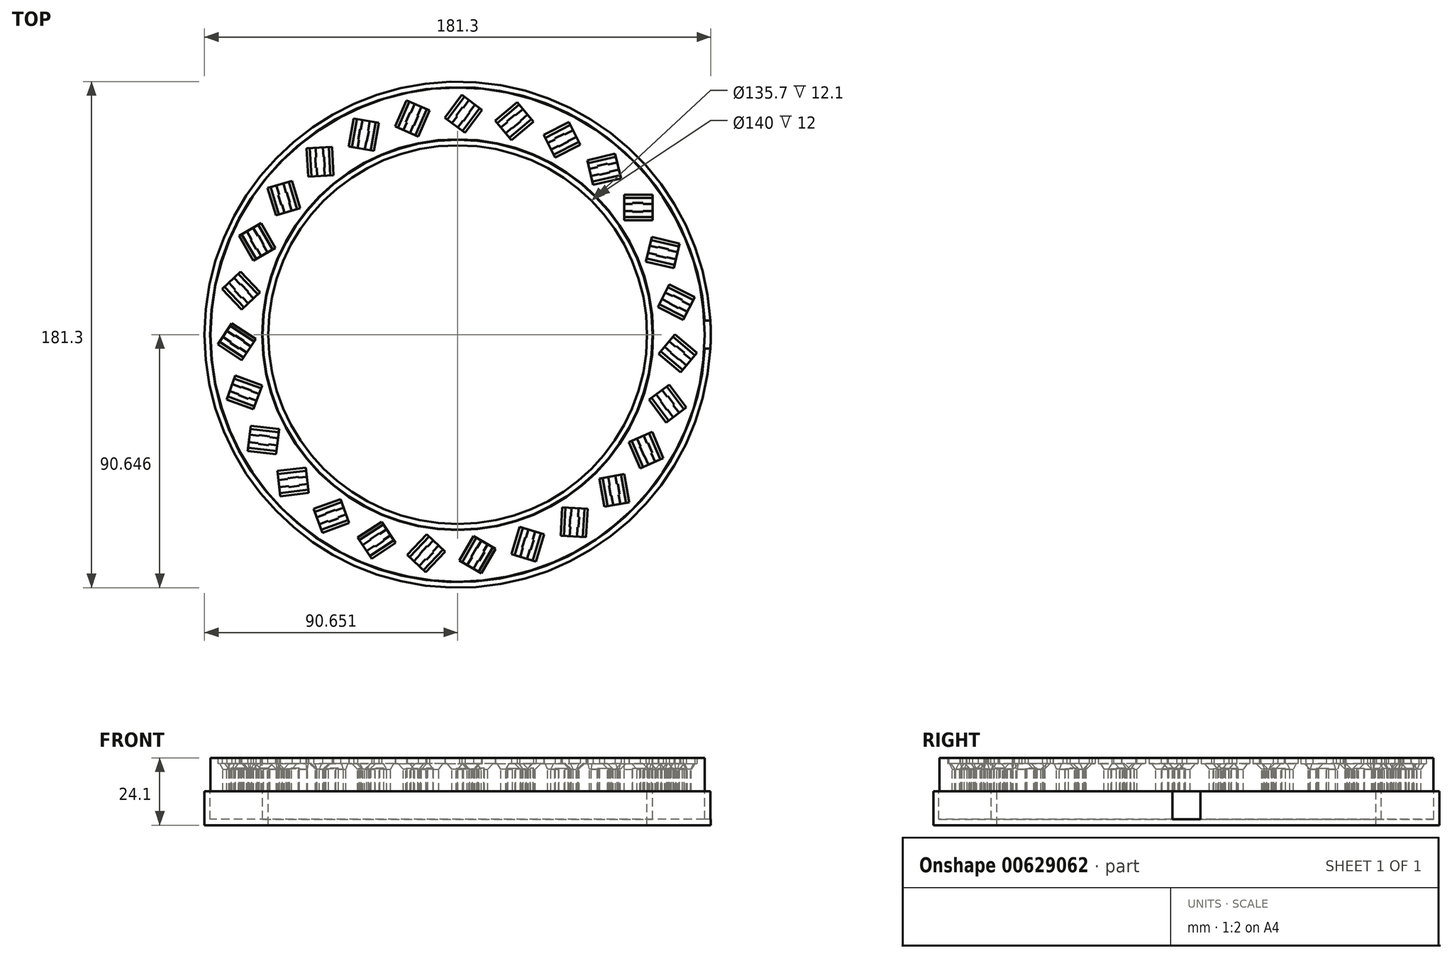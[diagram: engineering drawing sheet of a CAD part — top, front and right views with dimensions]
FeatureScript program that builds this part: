
annotation { "Feature Type Name" : "Feature", "Feature Type Description" : "" }
export const myFeature = defineFeature(function(context is Context, id is Id, definition is map)
    precondition{}
    {
        {
            var Q0;
            Q0=qCreatedBy(makeId("Top.planeOp"),FACE);
            var sketch = newSketch(context, id + "F0", { "sketchPlane" : qUnion([Q0])});
            skLineSegment(sketch, "E0.bottom", {"start": v(0, 0) * mm, "end": v(10.2, 0) * mm});
            skLineSegment(sketch, "E0.top", {"start": v(0, 9.1) * mm, "end": v(10.2, 9.1) * mm});
            skLineSegment(sketch, "E0.left", {"start": v(0, 0) * mm, "end": v(0, 9.1) * mm});
            skLineSegment(sketch, "E0.right", {"start": v(10.2, 0) * mm, "end": v(10.2, 9.1) * mm});
            skLineSegment(sketch, "E1.0", {"start": v(-3.5, 12.6) * mm, "end": v(13.7, 12.6) * mm});
            skLineSegment(sketch, "E1.1", {"start": v(-3.5, -3.5) * mm, "end": v(-3.5, 12.6) * mm});
            skLineSegment(sketch, "E1.2", {"start": v(-3.5, -3.5) * mm, "end": v(13.7, -3.5) * mm});
            skLineSegment(sketch, "E1.3", {"start": v(13.7, -3.5) * mm, "end": v(13.7, 12.6) * mm});
            skSolve(sketch);
        }
        {
            var Q0;
            Q0=makeQuery(id+"F0.imprint","IMPRINT",FACE,{"disambiguationData":[TD([[makeQuery(id+"F0.imprint","IMPRINT",EDGE,{"derivedFrom":sQuery(id+"F0.wireOp",EDGE,"E0.bottom")}),-1.0]])]});
            extrude(context, id + "F1", {"entities" : qUnion([Q0]), "depth" : 2 * mm, "offsetDistance" : 25 * mm});
        }
        {
            var Q0;
            Q0=makeQuery(id+"F1.opExtrude","CAP_FACE",FACE,{"disambiguationData":[OSD([sQuery(id+"F0.wireOp",EDGE,"E0.bottom"),sQuery(id+"F0.wireOp",EDGE,"E0.top"),sQuery(id+"F0.wireOp",EDGE,"E0.left"),sQuery(id+"F0.wireOp",EDGE,"E0.right"),sQuery(id+"F0.wireOp",EDGE,"E1.0"),sQuery(id+"F0.wireOp",EDGE,"E1.1"),sQuery(id+"F0.wireOp",EDGE,"E1.2"),sQuery(id+"F0.wireOp",EDGE,"E1.3")])],"isStart":true});
            var sketch = newSketch(context, id + "F2", { "sketchPlane" : qUnion([Q0])});
            skLineSegment(sketch, "E2.0", {"start": v(0, -5.85) * mm, "end": v(10.2, -5.85) * mm});
            skLineSegment(sketch, "E3.0", {"start": v(0, -3.25) * mm, "end": v(10.2, -3.25) * mm});
            skPoint(sketch, "E4.end.orphan", {"position": v(10.2, -4.55) * mm});
            skPoint(sketch, "E4.start.orphan", {"position": v(0, -4.55) * mm});
            skLineSegment(sketch, "E5.0", {"start": v(10.2, 0) * mm, "end": v(10.2, -9.1) * mm});
            skSolve(sketch);
        }
        {
            var Q0;
            {var subQ0=sQuery(id+"F2.wireOp",EDGE,"E3.0");Q0=makeQuery(id+"F2.imprint","IMPRINT",FACE,{"disambiguationData":[TD([[makeQuery(id+"F2.imprint","IMPRINT",EDGE,{"derivedFrom":subQ0}),1.0]])]});}
            var Q1;
            {var subQ0=sQuery(id+"F2.wireOp",EDGE,"E2.0");Q1=makeQuery(id+"F2.imprint","IMPRINT",FACE,{"disambiguationData":[TD([[makeQuery(id+"F2.imprint","IMPRINT",EDGE,{"derivedFrom":subQ0}),-1.0]])]});}
            var Q2;
            {var subQ1=makeQuery(id+"F1.opExtrude","CAP_EDGE",EDGE,{"disambiguationData":[OSD([sQuery(id+"F0.wireOp",EDGE,"E0.bottom")])],"isStart":true});Q2=makeQuery(id+"F2.imprint","IMPRINT",FACE,{"disambiguationData":[TD([[makeQuery(id+"F2.imprint","IMPRINT",EDGE,{"derivedFrom":subQ1}),1.0]])]});}
            extrude(context, id + "F3", {"entities" : qUnion([Q0, Q1, Q2]), "operationType" : NewBodyOperationType.ADD, "depth" : 10 * mm, "offsetDistance" : 25 * mm});
        }
        {
            var Q0;
            Q0=makeQuery(id+"F3.opExtrude","CAP_EDGE",EDGE,{"disambiguationData":[OSD([sQuery(id+"F2.wireOp",EDGE,"E3.0")])],"isStart":true});
            var Q1;
            Q1=makeQuery(id+"F3.opExtrude","CAP_EDGE",EDGE,{"disambiguationData":[OSD([sQuery(id+"F2.wireOp",EDGE,"E2.0")])],"isStart":true});
            chamfer(context, id + "F4", {"entities" : qUnion([Q0, Q1]), "width" : 2.1 * mm, "tangentPropagation" : true});
        }
        {
            var Q0;
            Q0=makeQuery(id+"F1.opExtrude","CAP_FACE",FACE,{"disambiguationData":[OSD([sQuery(id+"F0.wireOp",EDGE,"E0.bottom"),sQuery(id+"F0.wireOp",EDGE,"E0.top"),sQuery(id+"F0.wireOp",EDGE,"E0.left"),sQuery(id+"F0.wireOp",EDGE,"E0.right"),sQuery(id+"F0.wireOp",EDGE,"E1.0"),sQuery(id+"F0.wireOp",EDGE,"E1.1"),sQuery(id+"F0.wireOp",EDGE,"E1.2"),sQuery(id+"F0.wireOp",EDGE,"E1.3")])],"isStart":false});
            var sketch = newSketch(context, id + "F5", { "sketchPlane" : qUnion([Q0])});
            skLineSegment(sketch, "E6.bottom", {"start": v(3.03, 6.2) * mm, "end": v(6.78, 6.2) * mm});
            skLineSegment(sketch, "E6.top", {"start": v(3.03, 3) * mm, "end": v(6.78, 3) * mm});
            skLineSegment(sketch, "E6.left", {"start": v(3.03, 6.2) * mm, "end": v(3.03, 3) * mm});
            skLineSegment(sketch, "E6.right", {"start": v(6.78, 6.2) * mm, "end": v(6.78, 3) * mm});
            skLineSegment(sketch, "E7.0", {"start": v(10.2, 5.85) * mm, "end": v(0, 5.85) * mm});
            skSolve(sketch);
        }
        {
            var Q0;
            {var subQ0=sQuery(id+"F5.wireOp",EDGE,"E6.bottom");Q0=makeQuery(id+"F5.imprint","IMPRINT",FACE,{"disambiguationData":[TD([[makeQuery(id+"F5.imprint","IMPRINT",EDGE,{"derivedFrom":subQ0}),-1.0]])]});}
            var Q1;
            {var subQ0=sQuery(id+"F5.wireOp",EDGE,"E6.top");Q1=makeQuery(id+"F5.imprint","IMPRINT",FACE,{"disambiguationData":[TD([[makeQuery(id+"F5.imprint","IMPRINT",EDGE,{"derivedFrom":subQ0}),1.0]])]});}
            extrude(context, id + "F6", {"entities" : qUnion([Q0, Q1]), "operationType" : NewBodyOperationType.REMOVE, "oppositeDirection" : true, "depth" : 25 * mm, "offsetDistance" : 25 * mm});
        }
        {
            var Q0;
            Q0=makeQuery(id+"F1.opExtrude","CAP_FACE",FACE,{"disambiguationData":[OSD([sQuery(id+"F0.wireOp",EDGE,"E0.bottom"),sQuery(id+"F0.wireOp",EDGE,"E0.top"),sQuery(id+"F0.wireOp",EDGE,"E0.left"),sQuery(id+"F0.wireOp",EDGE,"E0.right"),sQuery(id+"F0.wireOp",EDGE,"E1.0"),sQuery(id+"F0.wireOp",EDGE,"E1.1"),sQuery(id+"F0.wireOp",EDGE,"E1.2"),sQuery(id+"F0.wireOp",EDGE,"E1.3")])],"isStart":false});
            var sketch = newSketch(context, id + "F7", { "sketchPlane" : qUnion([Q0])});
            skCircle(sketch, "E8", {"center": v(-59.6, -41.02) * mm, "radius": 67.5 * mm});
            skSolve(sketch);
        }
        {
            var Q0;
            Q0=makeQuery(id+"F1.opExtrude","SWEPT_BODY",BODY,{"disambiguationData":[OSD([sQuery(id+"F0.wireOp",EDGE,"E0.bottom"),sQuery(id+"F0.wireOp",EDGE,"E0.top"),sQuery(id+"F0.wireOp",EDGE,"E0.left"),sQuery(id+"F0.wireOp",EDGE,"E0.right"),sQuery(id+"F0.wireOp",EDGE,"E1.0"),sQuery(id+"F0.wireOp",EDGE,"E1.1"),sQuery(id+"F0.wireOp",EDGE,"E1.2"),sQuery(id+"F0.wireOp",EDGE,"E1.3")])]});
            var Q1;
            Q1=sQuery(id+"F7.wireOp",EDGE,"E8");
            circularPattern(context, id + "F8", {"entities" : qUnion([Q0]), "axis" : qUnion([Q1]), "angle" : 360 * degree, "instanceCount" : 27, "equalSpace" : true});
        }
        {
            var Q0;
            Q0=makeQuery(id+"F8.opPattern","COPY",FACE,{"derivedFrom":makeQuery(id+"F1.opExtrude","CAP_FACE",FACE,{"disambiguationData":[OSD([sQuery(id+"F0.wireOp",EDGE,"E0.bottom"),sQuery(id+"F0.wireOp",EDGE,"E0.top"),sQuery(id+"F0.wireOp",EDGE,"E0.left"),sQuery(id+"F0.wireOp",EDGE,"E0.right"),sQuery(id+"F0.wireOp",EDGE,"E1.0"),sQuery(id+"F0.wireOp",EDGE,"E1.1"),sQuery(id+"F0.wireOp",EDGE,"E1.2"),sQuery(id+"F0.wireOp",EDGE,"E1.3")])],"isStart":false}),"instanceName":"8"});
            var sketch = newSketch(context, id + "F9", { "sketchPlane" : qUnion([Q0])});
            skPoint(sketch, "E9.0", {"position": v(-59.6, -41.02) * mm});
            skPoint(sketch, "E10.0", {"position": v(-148.92, -24.5) * mm});
            skCircle(sketch, "E11", {"center": v(-59.6, -41.02) * mm, "radius": 90.83 * mm});
            skCircle(sketch, "E12.0", {"center": v(-59.6, -41.02) * mm, "radius": 67.5 * mm});
            skLineSegment(sketch, "E13.0.0", {"start": v(-111.65, 1.97) * mm, "end": v(-116.58, 18.44) * mm});
            skLineSegment(sketch, "E13.0.1", {"start": v(-116.58, 18.44) * mm, "end": v(-132, 13.83) * mm});
            skLineSegment(sketch, "E13.0.2", {"start": v(-132, 13.83) * mm, "end": v(-127.07, -2.65) * mm});
            skLineSegment(sketch, "E13.0.3", {"start": v(-127.07, -2.65) * mm, "end": v(-111.65, 1.97) * mm});
            skLineSegment(sketch, "E14.0.0", {"start": v(-120.16, -11.2) * mm, "end": v(-128.76, 3.7) * mm});
            skLineSegment(sketch, "E14.0.1", {"start": v(-128.76, 3.7) * mm, "end": v(-142.7, -4.35) * mm});
            skLineSegment(sketch, "E14.0.2", {"start": v(-142.7, -4.35) * mm, "end": v(-134.1, -19.24) * mm});
            skLineSegment(sketch, "E14.0.3", {"start": v(-134.1, -19.24) * mm, "end": v(-120.16, -11.2) * mm});
            skLineSegment(sketch, "E15.0.0", {"start": v(-125.4, -25.96) * mm, "end": v(-137.21, -13.45) * mm});
            skLineSegment(sketch, "E15.0.1", {"start": v(-137.21, -13.45) * mm, "end": v(-148.92, -24.5) * mm});
            skLineSegment(sketch, "E15.0.2", {"start": v(-148.92, -24.5) * mm, "end": v(-137.12, -37.01) * mm});
            skLineSegment(sketch, "E15.0.3", {"start": v(-137.12, -37.01) * mm, "end": v(-125.4, -25.96) * mm});
            skLineSegment(sketch, "E16.0.0", {"start": v(-127.1, -41.54) * mm, "end": v(-141.48, -32.1) * mm});
            skLineSegment(sketch, "E16.0.1", {"start": v(-141.48, -32.1) * mm, "end": v(-150.32, -45.54) * mm});
            skLineSegment(sketch, "E16.0.2", {"start": v(-150.32, -45.54) * mm, "end": v(-135.95, -55) * mm});
            skLineSegment(sketch, "E16.0.3", {"start": v(-135.95, -55) * mm, "end": v(-127.1, -41.54) * mm});
            skLineSegment(sketch, "E17.0.0", {"start": v(-125.17, -57.1) * mm, "end": v(-141.33, -51.21) * mm});
            skLineSegment(sketch, "E17.0.1", {"start": v(-141.33, -51.21) * mm, "end": v(-146.84, -66.34) * mm});
            skLineSegment(sketch, "E17.0.2", {"start": v(-146.84, -66.34) * mm, "end": v(-130.67, -72.22) * mm});
            skLineSegment(sketch, "E17.0.3", {"start": v(-130.67, -72.22) * mm, "end": v(-125.17, -57.1) * mm});
            skLineSegment(sketch, "E18.0.0", {"start": v(-119.7, -71.78) * mm, "end": v(-136.78, -69.78) * mm});
            skLineSegment(sketch, "E18.0.1", {"start": v(-136.78, -69.78) * mm, "end": v(-138.65, -85.78) * mm});
            skLineSegment(sketch, "E18.0.2", {"start": v(-138.65, -85.78) * mm, "end": v(-121.56, -87.77) * mm});
            skLineSegment(sketch, "E18.0.3", {"start": v(-121.56, -87.77) * mm, "end": v(-119.7, -71.78) * mm});
            skLineSegment(sketch, "E19.0.0", {"start": v(-110.98, -84.8) * mm, "end": v(-128.07, -86.8) * mm});
            skLineSegment(sketch, "E19.0.1", {"start": v(-128.07, -86.8) * mm, "end": v(-126.2, -102.8) * mm});
            skLineSegment(sketch, "E19.0.2", {"start": v(-126.2, -102.8) * mm, "end": v(-109.11, -100.8) * mm});
            skLineSegment(sketch, "E19.0.3", {"start": v(-109.11, -100.8) * mm, "end": v(-110.98, -84.8) * mm});
            skLineSegment(sketch, "E20.0.0", {"start": v(-99.5, -95.48) * mm, "end": v(-115.66, -101.36) * mm});
            skLineSegment(sketch, "E20.0.1", {"start": v(-115.66, -101.36) * mm, "end": v(-110.16, -116.49) * mm});
            skLineSegment(sketch, "E20.0.2", {"start": v(-110.16, -116.49) * mm, "end": v(-94, -110.6) * mm});
            skLineSegment(sketch, "E20.0.3", {"start": v(-94, -110.6) * mm, "end": v(-99.5, -95.48) * mm});
            skLineSegment(sketch, "E21.0.0", {"start": v(-85.87, -103.2) * mm, "end": v(-100.24, -112.66) * mm});
            skLineSegment(sketch, "E21.0.1", {"start": v(-100.24, -112.66) * mm, "end": v(-91.4, -126.11) * mm});
            skLineSegment(sketch, "E21.0.2", {"start": v(-91.4, -126.11) * mm, "end": v(-77.02, -116.66) * mm});
            skLineSegment(sketch, "E21.0.3", {"start": v(-77.02, -116.66) * mm, "end": v(-85.87, -103.2) * mm});
            skLineSegment(sketch, "E22.0.0", {"start": v(-70.82, -107.59) * mm, "end": v(-82.62, -120.1) * mm});
            skLineSegment(sketch, "E22.0.1", {"start": v(-82.62, -120.1) * mm, "end": v(-70.91, -131.15) * mm});
            skLineSegment(sketch, "E22.0.2", {"start": v(-70.91, -131.15) * mm, "end": v(-59.1, -118.64) * mm});
            skLineSegment(sketch, "E22.0.3", {"start": v(-59.1, -118.64) * mm, "end": v(-70.82, -107.59) * mm});
            skLineSegment(sketch, "E23.0.0", {"start": v(-55.17, -108.38) * mm, "end": v(-63.77, -123.27) * mm});
            skLineSegment(sketch, "E23.0.1", {"start": v(-63.77, -123.27) * mm, "end": v(-49.82, -131.32) * mm});
            skLineSegment(sketch, "E23.0.2", {"start": v(-49.82, -131.32) * mm, "end": v(-41.22, -116.43) * mm});
            skLineSegment(sketch, "E23.0.3", {"start": v(-41.22, -116.43) * mm, "end": v(-55.17, -108.38) * mm});
            skLineSegment(sketch, "E24.0.0", {"start": v(-39.75, -105.54) * mm, "end": v(-44.69, -122.02) * mm});
            skLineSegment(sketch, "E24.0.1", {"start": v(-44.69, -122.02) * mm, "end": v(-29.26, -126.63) * mm});
            skLineSegment(sketch, "E24.0.2", {"start": v(-29.26, -126.63) * mm, "end": v(-24.33, -110.16) * mm});
            skLineSegment(sketch, "E24.0.3", {"start": v(-24.33, -110.16) * mm, "end": v(-39.75, -105.54) * mm});
            skLineSegment(sketch, "E25.0.0", {"start": v(-25.41, -99.22) * mm, "end": v(-26.41, -116.4) * mm});
            skLineSegment(sketch, "E25.0.1", {"start": v(-26.41, -116.4) * mm, "end": v(-10.34, -117.33) * mm});
            skLineSegment(sketch, "E25.0.2", {"start": v(-10.34, -117.33) * mm, "end": v(-9.34, -100.16) * mm});
            skLineSegment(sketch, "E25.0.3", {"start": v(-9.34, -100.16) * mm, "end": v(-25.41, -99.22) * mm});
            skLineSegment(sketch, "E26.0.0", {"start": v(-12.91, -89.76) * mm, "end": v(-9.92, -106.7) * mm});
            skLineSegment(sketch, "E26.0.1", {"start": v(-9.92, -106.7) * mm, "end": v(5.93, -103.9) * mm});
            skLineSegment(sketch, "E26.0.2", {"start": v(5.93, -103.9) * mm, "end": v(2.94, -86.97) * mm});
            skLineSegment(sketch, "E26.0.3", {"start": v(2.94, -86.97) * mm, "end": v(-12.91, -89.76) * mm});
            skLineSegment(sketch, "E27.0.0", {"start": v(-2.93, -77.68) * mm, "end": v(3.88, -93.47) * mm});
            skLineSegment(sketch, "E27.0.1", {"start": v(3.88, -93.47) * mm, "end": v(18.67, -87.1) * mm});
            skLineSegment(sketch, "E27.0.2", {"start": v(18.67, -87.1) * mm, "end": v(11.85, -71.3) * mm});
            skLineSegment(sketch, "E27.0.3", {"start": v(11.85, -71.3) * mm, "end": v(-2.93, -77.68) * mm});
            skLineSegment(sketch, "E28.0.0", {"start": v(4, -63.62) * mm, "end": v(14.27, -77.42) * mm});
            skLineSegment(sketch, "E28.0.1", {"start": v(14.27, -77.42) * mm, "end": v(27.18, -67.8) * mm});
            skLineSegment(sketch, "E28.0.2", {"start": v(27.18, -67.8) * mm, "end": v(16.91, -54) * mm});
            skLineSegment(sketch, "E28.0.3", {"start": v(16.91, -54) * mm, "end": v(4, -63.62) * mm});
            skLineSegment(sketch, "E29.0.0", {"start": v(7.5, -48.34) * mm, "end": v(20.67, -59.4) * mm});
            skLineSegment(sketch, "E29.0.1", {"start": v(20.67, -59.4) * mm, "end": v(31.02, -47.07) * mm});
            skLineSegment(sketch, "E29.0.2", {"start": v(31.02, -47.07) * mm, "end": v(17.84, -36.01) * mm});
            skLineSegment(sketch, "E29.0.3", {"start": v(17.84, -36.01) * mm, "end": v(7.5, -48.34) * mm});
            skLineSegment(sketch, "E30.0.0", {"start": v(-3.5, 12.6) * mm, "end": v(-3.5, -3.5) * mm});
            skLineSegment(sketch, "E30.0.1", {"start": v(-3.5, -3.5) * mm, "end": v(13.7, -3.5) * mm});
            skLineSegment(sketch, "E30.0.2", {"start": v(13.7, -3.5) * mm, "end": v(13.7, 12.6) * mm});
            skLineSegment(sketch, "E30.0.3", {"start": v(13.7, 12.6) * mm, "end": v(-3.5, 12.6) * mm});
            skLineSegment(sketch, "E31.0.0", {"start": v(-13.67, 8.43) * mm, "end": v(3.07, 12.4) * mm});
            skLineSegment(sketch, "E31.0.1", {"start": v(3.07, 12.4) * mm, "end": v(-0.64, 28.06) * mm});
            skLineSegment(sketch, "E31.0.2", {"start": v(-0.64, 28.06) * mm, "end": v(-17.38, 24.1) * mm});
            skLineSegment(sketch, "E31.0.3", {"start": v(-17.38, 24.1) * mm, "end": v(-13.67, 8.43) * mm});
            skLineSegment(sketch, "E32.0.0", {"start": v(-26.3, 17.7) * mm, "end": v(-10.94, 25.4) * mm});
            skLineSegment(sketch, "E32.0.1", {"start": v(-10.94, 25.4) * mm, "end": v(-18.16, 39.8) * mm});
            skLineSegment(sketch, "E32.0.2", {"start": v(-18.16, 39.8) * mm, "end": v(-33.53, 32.08) * mm});
            skLineSegment(sketch, "E32.0.3", {"start": v(-33.53, 32.08) * mm, "end": v(-26.3, 17.7) * mm});
            skLineSegment(sketch, "E33.0.0", {"start": v(-40.75, 23.79) * mm, "end": v(-27.57, 34.84) * mm});
            skLineSegment(sketch, "E33.0.1", {"start": v(-27.57, 34.84) * mm, "end": v(-37.92, 47.18) * mm});
            skLineSegment(sketch, "E33.0.2", {"start": v(-37.92, 47.18) * mm, "end": v(-51.1, 36.12) * mm});
            skLineSegment(sketch, "E33.0.3", {"start": v(-51.1, 36.12) * mm, "end": v(-40.75, 23.79) * mm});
            skLineSegment(sketch, "E34.0.0", {"start": v(-56.2, 26.39) * mm, "end": v(-45.93, 40.19) * mm});
            skLineSegment(sketch, "E34.0.1", {"start": v(-45.93, 40.19) * mm, "end": v(-58.84, 49.8) * mm});
            skLineSegment(sketch, "E34.0.2", {"start": v(-58.84, 49.8) * mm, "end": v(-69.12, 36) * mm});
            skLineSegment(sketch, "E34.0.3", {"start": v(-69.12, 36) * mm, "end": v(-56.2, 26.39) * mm});
            skLineSegment(sketch, "E35.0.0", {"start": v(-71.84, 25.36) * mm, "end": v(-65.03, 41.15) * mm});
            skLineSegment(sketch, "E35.0.1", {"start": v(-65.03, 41.15) * mm, "end": v(-79.81, 47.53) * mm});
            skLineSegment(sketch, "E35.0.2", {"start": v(-79.81, 47.53) * mm, "end": v(-86.62, 31.74) * mm});
            skLineSegment(sketch, "E35.0.3", {"start": v(-86.62, 31.74) * mm, "end": v(-71.84, 25.36) * mm});
            skLineSegment(sketch, "E36.0.0", {"start": v(-86.82, 20.75) * mm, "end": v(-83.83, 37.69) * mm});
            skLineSegment(sketch, "E36.0.1", {"start": v(-83.83, 37.69) * mm, "end": v(-99.69, 40.48) * mm});
            skLineSegment(sketch, "E36.0.2", {"start": v(-99.69, 40.48) * mm, "end": v(-102.68, 23.54) * mm});
            skLineSegment(sketch, "E36.0.3", {"start": v(-102.68, 23.54) * mm, "end": v(-86.82, 20.75) * mm});
            skLineSegment(sketch, "E37.0.0", {"start": v(-100.33, 12.8) * mm, "end": v(-101.33, 29.98) * mm});
            skLineSegment(sketch, "E37.0.1", {"start": v(-101.33, 29.98) * mm, "end": v(-117.4, 29.04) * mm});
            skLineSegment(sketch, "E37.0.2", {"start": v(-117.4, 29.04) * mm, "end": v(-116.4, 11.87) * mm});
            skLineSegment(sketch, "E37.0.3", {"start": v(-116.4, 11.87) * mm, "end": v(-100.33, 12.8) * mm});
            skLineSegment(sketch, "E38.0.0", {"start": v(7.37, -32.67) * mm, "end": v(22.74, -40.4) * mm});
            skLineSegment(sketch, "E38.0.1", {"start": v(22.74, -40.4) * mm, "end": v(29.97, -26) * mm});
            skLineSegment(sketch, "E38.0.2", {"start": v(29.97, -26) * mm, "end": v(14.6, -18.29) * mm});
            skLineSegment(sketch, "E38.0.3", {"start": v(14.6, -18.29) * mm, "end": v(7.37, -32.67) * mm});
            skLineSegment(sketch, "E39.0.0", {"start": v(3.64, -17.45) * mm, "end": v(20.38, -21.42) * mm});
            skLineSegment(sketch, "E39.0.1", {"start": v(20.38, -21.42) * mm, "end": v(24.1, -5.75) * mm});
            skLineSegment(sketch, "E39.0.2", {"start": v(24.1, -5.75) * mm, "end": v(7.35, -1.79) * mm});
            skLineSegment(sketch, "E39.0.3", {"start": v(7.35, -1.79) * mm, "end": v(3.64, -17.45) * mm});
            skSolve(sketch);
        }
        {
            var Q0;
            {var subQ1=sQuery(id+"F9.wireOp",EDGE,"E19.0.2");Q0=makeQuery(id+"F9.imprint","IMPRINT",FACE,{"disambiguationData":[TD([[makeQuery(id+"F9.imprint","IMPRINT",EDGE,{"derivedFrom":subQ1}),-1.0]])]});}
            var Q1;
            {var subQ3=sQuery(id+"F9.wireOp",EDGE,"E18.0.2");Q1=makeQuery(id+"F9.imprint","IMPRINT",FACE,{"disambiguationData":[TD([[makeQuery(id+"F9.imprint","IMPRINT",EDGE,{"derivedFrom":subQ3}),-1.0]])]});}
            var Q2;
            {var subQ0=sQuery(id+"F9.wireOp",EDGE,"E17.0.2");Q2=makeQuery(id+"F9.imprint","IMPRINT",FACE,{"disambiguationData":[TD([[makeQuery(id+"F9.imprint","IMPRINT",EDGE,{"derivedFrom":subQ0}),-1.0]])]});}
            var Q3;
            {var subQ1=sQuery(id+"F9.wireOp",EDGE,"E16.0.2");Q3=makeQuery(id+"F9.imprint","IMPRINT",FACE,{"disambiguationData":[TD([[makeQuery(id+"F9.imprint","IMPRINT",EDGE,{"derivedFrom":subQ1}),-1.0]])]});}
            var Q4;
            {var subQ1=sQuery(id+"F9.wireOp",EDGE,"E15.0.2");Q4=makeQuery(id+"F9.imprint","IMPRINT",FACE,{"disambiguationData":[TD([[makeQuery(id+"F9.imprint","IMPRINT",EDGE,{"derivedFrom":subQ1}),-1.0]])]});}
            var Q5;
            {var subQ1=sQuery(id+"F9.wireOp",EDGE,"E14.0.2");Q5=makeQuery(id+"F9.imprint","IMPRINT",FACE,{"disambiguationData":[TD([[makeQuery(id+"F9.imprint","IMPRINT",EDGE,{"derivedFrom":subQ1}),-1.0]])]});}
            var Q6;
            {var subQ1=sQuery(id+"F9.wireOp",EDGE,"E13.0.2");Q6=makeQuery(id+"F9.imprint","IMPRINT",FACE,{"disambiguationData":[TD([[makeQuery(id+"F9.imprint","IMPRINT",EDGE,{"derivedFrom":subQ1}),1.0]])]});}
            var Q7;
            {var subQ1=sQuery(id+"F9.wireOp",EDGE,"E13.0.0");Q7=makeQuery(id+"F9.imprint","IMPRINT",FACE,{"disambiguationData":[TD([[makeQuery(id+"F9.imprint","IMPRINT",EDGE,{"derivedFrom":subQ1}),-1.0]])]});}
            var Q8;
            {var subQ1=sQuery(id+"F9.wireOp",EDGE,"E36.0.2");Q8=makeQuery(id+"F9.imprint","IMPRINT",FACE,{"disambiguationData":[TD([[makeQuery(id+"F9.imprint","IMPRINT",EDGE,{"derivedFrom":subQ1}),-1.0]])]});}
            var Q9;
            {var subQ1=sQuery(id+"F9.wireOp",EDGE,"E35.0.2");Q9=makeQuery(id+"F9.imprint","IMPRINT",FACE,{"disambiguationData":[TD([[makeQuery(id+"F9.imprint","IMPRINT",EDGE,{"derivedFrom":subQ1}),-1.0]])]});}
            var Q10;
            {var subQ1=sQuery(id+"F9.wireOp",EDGE,"E34.0.2");Q10=makeQuery(id+"F9.imprint","IMPRINT",FACE,{"disambiguationData":[TD([[makeQuery(id+"F9.imprint","IMPRINT",EDGE,{"derivedFrom":subQ1}),-1.0]])]});}
            var Q11;
            {var subQ1=sQuery(id+"F9.wireOp",EDGE,"E33.0.2");Q11=makeQuery(id+"F9.imprint","IMPRINT",FACE,{"disambiguationData":[TD([[makeQuery(id+"F9.imprint","IMPRINT",EDGE,{"derivedFrom":subQ1}),-1.0]])]});}
            var Q12;
            {var subQ0=sQuery(id+"F9.wireOp",EDGE,"E32.0.2");Q12=makeQuery(id+"F9.imprint","IMPRINT",FACE,{"disambiguationData":[TD([[makeQuery(id+"F9.imprint","IMPRINT",EDGE,{"derivedFrom":subQ0}),-1.0]])]});}
            var Q13;
            {var subQ1=sQuery(id+"F9.wireOp",EDGE,"E31.0.2");Q13=makeQuery(id+"F9.imprint","IMPRINT",FACE,{"disambiguationData":[TD([[makeQuery(id+"F9.imprint","IMPRINT",EDGE,{"derivedFrom":subQ1}),-1.0]])]});}
            var Q14;
            {var subQ1=sQuery(id+"F9.wireOp",EDGE,"E30.0.0");Q14=makeQuery(id+"F9.imprint","IMPRINT",FACE,{"disambiguationData":[TD([[makeQuery(id+"F9.imprint","IMPRINT",EDGE,{"derivedFrom":subQ1}),-1.0]])]});}
            var Q15;
            {var subQ1=sQuery(id+"F9.wireOp",EDGE,"E29.0.2");Q15=makeQuery(id+"F9.imprint","IMPRINT",FACE,{"disambiguationData":[TD([[makeQuery(id+"F9.imprint","IMPRINT",EDGE,{"derivedFrom":subQ1}),-1.0]])]});}
            var Q16;
            {var subQ3=sQuery(id+"F9.wireOp",EDGE,"E28.0.2");Q16=makeQuery(id+"F9.imprint","IMPRINT",FACE,{"disambiguationData":[TD([[makeQuery(id+"F9.imprint","IMPRINT",EDGE,{"derivedFrom":subQ3}),-1.0]])]});}
            var Q17;
            {var subQ0=sQuery(id+"F9.wireOp",EDGE,"E27.0.2");Q17=makeQuery(id+"F9.imprint","IMPRINT",FACE,{"disambiguationData":[TD([[makeQuery(id+"F9.imprint","IMPRINT",EDGE,{"derivedFrom":subQ0}),-1.0]])]});}
            var Q18;
            {var subQ1=sQuery(id+"F9.wireOp",EDGE,"E26.0.2");Q18=makeQuery(id+"F9.imprint","IMPRINT",FACE,{"disambiguationData":[TD([[makeQuery(id+"F9.imprint","IMPRINT",EDGE,{"derivedFrom":subQ1}),-1.0]])]});}
            var Q19;
            {var subQ1=sQuery(id+"F9.wireOp",EDGE,"E25.0.2");Q19=makeQuery(id+"F9.imprint","IMPRINT",FACE,{"disambiguationData":[TD([[makeQuery(id+"F9.imprint","IMPRINT",EDGE,{"derivedFrom":subQ1}),-1.0]])]});}
            var Q20;
            {var subQ1=sQuery(id+"F9.wireOp",EDGE,"E24.0.2");Q20=makeQuery(id+"F9.imprint","IMPRINT",FACE,{"disambiguationData":[TD([[makeQuery(id+"F9.imprint","IMPRINT",EDGE,{"derivedFrom":subQ1}),-1.0]])]});}
            var Q21;
            {var subQ1=sQuery(id+"F9.wireOp",EDGE,"E23.0.2");Q21=makeQuery(id+"F9.imprint","IMPRINT",FACE,{"disambiguationData":[TD([[makeQuery(id+"F9.imprint","IMPRINT",EDGE,{"derivedFrom":subQ1}),-1.0]])]});}
            var Q22;
            {var subQ0=sQuery(id+"F9.wireOp",EDGE,"E22.0.2");Q22=makeQuery(id+"F9.imprint","IMPRINT",FACE,{"disambiguationData":[TD([[makeQuery(id+"F9.imprint","IMPRINT",EDGE,{"derivedFrom":subQ0}),-1.0]])]});}
            var Q23;
            {var subQ1=sQuery(id+"F9.wireOp",EDGE,"E21.0.2");Q23=makeQuery(id+"F9.imprint","IMPRINT",FACE,{"disambiguationData":[TD([[makeQuery(id+"F9.imprint","IMPRINT",EDGE,{"derivedFrom":subQ1}),-1.0]])]});}
            var Q24;
            {var subQ1=sQuery(id+"F9.wireOp",EDGE,"E20.0.2");Q24=makeQuery(id+"F9.imprint","IMPRINT",FACE,{"disambiguationData":[TD([[makeQuery(id+"F9.imprint","IMPRINT",EDGE,{"derivedFrom":subQ1}),-1.0]])]});}
            var Q25;
            {var subQ3=sQuery(id+"F9.wireOp",EDGE,"E30.0.2");Q25=makeQuery(id+"F9.imprint","IMPRINT",FACE,{"disambiguationData":[TD([[makeQuery(id+"F9.imprint","IMPRINT",EDGE,{"derivedFrom":subQ3}),-1.0]])]});}
            var Q26;
            {var subQ3=sQuery(id+"F9.wireOp",EDGE,"E39.0.1");Q26=makeQuery(id+"F9.imprint","IMPRINT",FACE,{"disambiguationData":[TD([[makeQuery(id+"F9.imprint","IMPRINT",EDGE,{"derivedFrom":subQ3}),-1.0]])]});}
            var Q27;
            {var subQ0=sQuery(id+"F9.wireOp",EDGE,"E38.0.3");var subQ3=sQuery(id+"F9.wireOp",EDGE,"E39.0.0");var subQ5=makeQuery(id+"F9.imprint","INTERSECT",VERTEX,{"derivedFrom":[subQ0,subQ3]});Q27=makeQuery(id+"F9.imprint","IMPRINT",FACE,{"disambiguationData":[TD([[makeQuery(id+"F9.imprint","IMPRINT",EDGE,{"disambiguationData":[TD([[subQ5,-1.0]])],"derivedFrom":subQ0}),-1.0]])]});}
            var Q28;
            {var subQ0=sQuery(id+"F9.wireOp",EDGE,"E29.0.3");var subQ3=sQuery(id+"F9.wireOp",EDGE,"E38.0.0");var subQ5=makeQuery(id+"F9.imprint","INTERSECT",VERTEX,{"derivedFrom":[subQ0,subQ3]});Q28=makeQuery(id+"F9.imprint","IMPRINT",FACE,{"disambiguationData":[TD([[makeQuery(id+"F9.imprint","IMPRINT",EDGE,{"disambiguationData":[TD([[subQ5,-1.0]])],"derivedFrom":subQ0}),-1.0]])]});}
            var Q29;
            {var subQ0=sQuery(id+"F9.wireOp",EDGE,"E31.0.0");var subQ3=sQuery(id+"F9.wireOp",EDGE,"E30.0.0");var subQ5=makeQuery(id+"F9.imprint","INTERSECT",VERTEX,{"derivedFrom":[subQ0,subQ3]});Q29=makeQuery(id+"F9.imprint","IMPRINT",FACE,{"disambiguationData":[TD([[makeQuery(id+"F9.imprint","IMPRINT",EDGE,{"disambiguationData":[TD([[subQ5,1.0]])],"derivedFrom":subQ0}),-1.0]])]});}
            var Q30;
            {var subQ0=sQuery(id+"F9.wireOp",EDGE,"E31.0.1");Q30=makeQuery(id+"F9.imprint","IMPRINT",FACE,{"disambiguationData":[TD([[makeQuery(id+"F9.imprint","IMPRINT",EDGE,{"derivedFrom":subQ0}),-1.0]])]});}
            var Q31;
            {var subQ0=sQuery(id+"F9.wireOp",EDGE,"E39.0.3");var subQ3=sQuery(id+"F9.wireOp",EDGE,"E30.0.1");var subQ5=makeQuery(id+"F9.imprint","INTERSECT",VERTEX,{"derivedFrom":[subQ0,subQ3]});Q31=makeQuery(id+"F9.imprint","IMPRINT",FACE,{"disambiguationData":[TD([[makeQuery(id+"F9.imprint","IMPRINT",EDGE,{"disambiguationData":[TD([[subQ5,-1.0]])],"derivedFrom":subQ0}),-1.0]])]});}
            var Q32;
            {var subQ0=sQuery(id+"F9.wireOp",EDGE,"E13.0.1");Q32=makeQuery(id+"F9.imprint","IMPRINT",FACE,{"disambiguationData":[TD([[makeQuery(id+"F9.imprint","IMPRINT",EDGE,{"derivedFrom":subQ0}),-1.0]])]});}
            var Q33;
            {var subQ0=sQuery(id+"F9.wireOp",EDGE,"E13.0.3");var subQ3=sQuery(id+"F9.wireOp",EDGE,"E14.0.0");var subQ5=makeQuery(id+"F9.imprint","INTERSECT",VERTEX,{"derivedFrom":[subQ0,subQ3]});Q33=makeQuery(id+"F9.imprint","IMPRINT",FACE,{"disambiguationData":[TD([[makeQuery(id+"F9.imprint","IMPRINT",EDGE,{"disambiguationData":[TD([[subQ5,1.0]])],"derivedFrom":subQ0}),1.0]])]});}
            var Q34;
            {var subQ0=sQuery(id+"F9.wireOp",EDGE,"E14.0.3");var subQ3=sQuery(id+"F9.wireOp",EDGE,"E15.0.0");var subQ5=makeQuery(id+"F9.imprint","INTERSECT",VERTEX,{"derivedFrom":[subQ0,subQ3]});Q34=makeQuery(id+"F9.imprint","IMPRINT",FACE,{"disambiguationData":[TD([[makeQuery(id+"F9.imprint","IMPRINT",EDGE,{"disambiguationData":[TD([[subQ5,-1.0]])],"derivedFrom":subQ0}),-1.0]])]});}
            var Q35;
            {var subQ0=sQuery(id+"F9.wireOp",EDGE,"E15.0.3");var subQ3=sQuery(id+"F9.wireOp",EDGE,"E16.0.0");var subQ5=makeQuery(id+"F9.imprint","INTERSECT",VERTEX,{"derivedFrom":[subQ0,subQ3]});Q35=makeQuery(id+"F9.imprint","IMPRINT",FACE,{"disambiguationData":[TD([[makeQuery(id+"F9.imprint","IMPRINT",EDGE,{"disambiguationData":[TD([[subQ5,-1.0]])],"derivedFrom":subQ0}),-1.0]])]});}
            var Q36;
            {var subQ0=sQuery(id+"F9.wireOp",EDGE,"E16.0.3");var subQ3=sQuery(id+"F9.wireOp",EDGE,"E17.0.0");var subQ5=makeQuery(id+"F9.imprint","INTERSECT",VERTEX,{"derivedFrom":[subQ0,subQ3]});Q36=makeQuery(id+"F9.imprint","IMPRINT",FACE,{"disambiguationData":[TD([[makeQuery(id+"F9.imprint","IMPRINT",EDGE,{"disambiguationData":[TD([[subQ5,-1.0]])],"derivedFrom":subQ0}),-1.0]])]});}
            var Q37;
            {var subQ0=sQuery(id+"F9.wireOp",EDGE,"E17.0.3");var subQ3=sQuery(id+"F9.wireOp",EDGE,"E18.0.0");var subQ5=makeQuery(id+"F9.imprint","INTERSECT",VERTEX,{"derivedFrom":[subQ0,subQ3]});Q37=makeQuery(id+"F9.imprint","IMPRINT",FACE,{"disambiguationData":[TD([[makeQuery(id+"F9.imprint","IMPRINT",EDGE,{"disambiguationData":[TD([[subQ5,-1.0]])],"derivedFrom":subQ0}),-1.0]])]});}
            var Q38;
            {var subQ0=sQuery(id+"F9.wireOp",EDGE,"E18.0.3");var subQ3=sQuery(id+"F9.wireOp",EDGE,"E19.0.0");var subQ5=makeQuery(id+"F9.imprint","INTERSECT",VERTEX,{"derivedFrom":[subQ0,subQ3]});Q38=makeQuery(id+"F9.imprint","IMPRINT",FACE,{"disambiguationData":[TD([[makeQuery(id+"F9.imprint","IMPRINT",EDGE,{"disambiguationData":[TD([[subQ5,-1.0]])],"derivedFrom":subQ0}),-1.0]])]});}
            var Q39;
            {var subQ0=sQuery(id+"F9.wireOp",EDGE,"E19.0.3");var subQ3=sQuery(id+"F9.wireOp",EDGE,"E20.0.0");var subQ5=makeQuery(id+"F9.imprint","INTERSECT",VERTEX,{"derivedFrom":[subQ0,subQ3]});Q39=makeQuery(id+"F9.imprint","IMPRINT",FACE,{"disambiguationData":[TD([[makeQuery(id+"F9.imprint","IMPRINT",EDGE,{"disambiguationData":[TD([[subQ5,-1.0]])],"derivedFrom":subQ0}),-1.0]])]});}
            var Q40;
            {var subQ0=sQuery(id+"F9.wireOp",EDGE,"E20.0.3");var subQ3=sQuery(id+"F9.wireOp",EDGE,"E21.0.0");var subQ5=makeQuery(id+"F9.imprint","INTERSECT",VERTEX,{"derivedFrom":[subQ0,subQ3]});Q40=makeQuery(id+"F9.imprint","IMPRINT",FACE,{"disambiguationData":[TD([[makeQuery(id+"F9.imprint","IMPRINT",EDGE,{"disambiguationData":[TD([[subQ5,-1.0]])],"derivedFrom":subQ0}),-1.0]])]});}
            var Q41;
            {var subQ0=sQuery(id+"F9.wireOp",EDGE,"E21.0.3");var subQ3=sQuery(id+"F9.wireOp",EDGE,"E22.0.0");var subQ5=makeQuery(id+"F9.imprint","INTERSECT",VERTEX,{"derivedFrom":[subQ0,subQ3]});Q41=makeQuery(id+"F9.imprint","IMPRINT",FACE,{"disambiguationData":[TD([[makeQuery(id+"F9.imprint","IMPRINT",EDGE,{"disambiguationData":[TD([[subQ5,-1.0]])],"derivedFrom":subQ0}),-1.0]])]});}
            var Q42;
            {var subQ0=sQuery(id+"F9.wireOp",EDGE,"E36.0.3");var subQ3=sQuery(id+"F9.wireOp",EDGE,"E37.0.0");var subQ5=makeQuery(id+"F9.imprint","INTERSECT",VERTEX,{"derivedFrom":[subQ0,subQ3]});Q42=makeQuery(id+"F9.imprint","IMPRINT",FACE,{"disambiguationData":[TD([[makeQuery(id+"F9.imprint","IMPRINT",EDGE,{"disambiguationData":[TD([[subQ5,-1.0]])],"derivedFrom":subQ0}),-1.0]])]});}
            var Q43;
            {var subQ0=sQuery(id+"F9.wireOp",EDGE,"E35.0.3");var subQ3=sQuery(id+"F9.wireOp",EDGE,"E36.0.0");var subQ5=makeQuery(id+"F9.imprint","INTERSECT",VERTEX,{"derivedFrom":[subQ0,subQ3]});Q43=makeQuery(id+"F9.imprint","IMPRINT",FACE,{"disambiguationData":[TD([[makeQuery(id+"F9.imprint","IMPRINT",EDGE,{"disambiguationData":[TD([[subQ5,-1.0]])],"derivedFrom":subQ0}),-1.0]])]});}
            var Q44;
            {var subQ0=sQuery(id+"F9.wireOp",EDGE,"E34.0.3");var subQ3=sQuery(id+"F9.wireOp",EDGE,"E35.0.0");var subQ5=makeQuery(id+"F9.imprint","INTERSECT",VERTEX,{"derivedFrom":[subQ0,subQ3]});Q44=makeQuery(id+"F9.imprint","IMPRINT",FACE,{"disambiguationData":[TD([[makeQuery(id+"F9.imprint","IMPRINT",EDGE,{"disambiguationData":[TD([[subQ5,-1.0]])],"derivedFrom":subQ0}),-1.0]])]});}
            var Q45;
            {var subQ0=sQuery(id+"F9.wireOp",EDGE,"E33.0.3");var subQ3=sQuery(id+"F9.wireOp",EDGE,"E34.0.0");var subQ5=makeQuery(id+"F9.imprint","INTERSECT",VERTEX,{"derivedFrom":[subQ0,subQ3]});Q45=makeQuery(id+"F9.imprint","IMPRINT",FACE,{"disambiguationData":[TD([[makeQuery(id+"F9.imprint","IMPRINT",EDGE,{"disambiguationData":[TD([[subQ5,-1.0]])],"derivedFrom":subQ0}),-1.0]])]});}
            var Q46;
            {var subQ0=sQuery(id+"F9.wireOp",EDGE,"E32.0.3");var subQ3=sQuery(id+"F9.wireOp",EDGE,"E33.0.0");var subQ5=makeQuery(id+"F9.imprint","INTERSECT",VERTEX,{"derivedFrom":[subQ0,subQ3]});Q46=makeQuery(id+"F9.imprint","IMPRINT",FACE,{"disambiguationData":[TD([[makeQuery(id+"F9.imprint","IMPRINT",EDGE,{"disambiguationData":[TD([[subQ5,-1.0]])],"derivedFrom":subQ0}),-1.0]])]});}
            var Q47;
            {var subQ0=sQuery(id+"F9.wireOp",EDGE,"E31.0.3");var subQ3=sQuery(id+"F9.wireOp",EDGE,"E32.0.0");var subQ5=makeQuery(id+"F9.imprint","INTERSECT",VERTEX,{"derivedFrom":[subQ0,subQ3]});Q47=makeQuery(id+"F9.imprint","IMPRINT",FACE,{"disambiguationData":[TD([[makeQuery(id+"F9.imprint","IMPRINT",EDGE,{"disambiguationData":[TD([[subQ5,-1.0]])],"derivedFrom":subQ0}),-1.0]])]});}
            var Q48;
            {var subQ0=sQuery(id+"F9.wireOp",EDGE,"E28.0.3");var subQ3=sQuery(id+"F9.wireOp",EDGE,"E29.0.0");var subQ5=makeQuery(id+"F9.imprint","INTERSECT",VERTEX,{"derivedFrom":[subQ0,subQ3]});Q48=makeQuery(id+"F9.imprint","IMPRINT",FACE,{"disambiguationData":[TD([[makeQuery(id+"F9.imprint","IMPRINT",EDGE,{"disambiguationData":[TD([[subQ5,-1.0]])],"derivedFrom":subQ0}),-1.0]])]});}
            var Q49;
            {var subQ0=sQuery(id+"F9.wireOp",EDGE,"E27.0.3");var subQ3=sQuery(id+"F9.wireOp",EDGE,"E28.0.0");var subQ5=makeQuery(id+"F9.imprint","INTERSECT",VERTEX,{"derivedFrom":[subQ0,subQ3]});Q49=makeQuery(id+"F9.imprint","IMPRINT",FACE,{"disambiguationData":[TD([[makeQuery(id+"F9.imprint","IMPRINT",EDGE,{"disambiguationData":[TD([[subQ5,-1.0]])],"derivedFrom":subQ0}),-1.0]])]});}
            var Q50;
            {var subQ0=sQuery(id+"F9.wireOp",EDGE,"E26.0.3");var subQ3=sQuery(id+"F9.wireOp",EDGE,"E27.0.0");var subQ5=makeQuery(id+"F9.imprint","INTERSECT",VERTEX,{"derivedFrom":[subQ0,subQ3]});Q50=makeQuery(id+"F9.imprint","IMPRINT",FACE,{"disambiguationData":[TD([[makeQuery(id+"F9.imprint","IMPRINT",EDGE,{"disambiguationData":[TD([[subQ5,-1.0]])],"derivedFrom":subQ0}),-1.0]])]});}
            var Q51;
            {var subQ0=sQuery(id+"F9.wireOp",EDGE,"E25.0.3");var subQ3=sQuery(id+"F9.wireOp",EDGE,"E26.0.0");var subQ5=makeQuery(id+"F9.imprint","INTERSECT",VERTEX,{"derivedFrom":[subQ0,subQ3]});Q51=makeQuery(id+"F9.imprint","IMPRINT",FACE,{"disambiguationData":[TD([[makeQuery(id+"F9.imprint","IMPRINT",EDGE,{"disambiguationData":[TD([[subQ5,-1.0]])],"derivedFrom":subQ0}),-1.0]])]});}
            var Q52;
            {var subQ0=sQuery(id+"F9.wireOp",EDGE,"E24.0.3");var subQ3=sQuery(id+"F9.wireOp",EDGE,"E25.0.0");var subQ5=makeQuery(id+"F9.imprint","INTERSECT",VERTEX,{"derivedFrom":[subQ0,subQ3]});Q52=makeQuery(id+"F9.imprint","IMPRINT",FACE,{"disambiguationData":[TD([[makeQuery(id+"F9.imprint","IMPRINT",EDGE,{"disambiguationData":[TD([[subQ5,-1.0]])],"derivedFrom":subQ0}),-1.0]])]});}
            var Q53;
            {var subQ0=sQuery(id+"F9.wireOp",EDGE,"E23.0.3");var subQ3=sQuery(id+"F9.wireOp",EDGE,"E24.0.0");var subQ5=makeQuery(id+"F9.imprint","INTERSECT",VERTEX,{"derivedFrom":[subQ0,subQ3]});Q53=makeQuery(id+"F9.imprint","IMPRINT",FACE,{"disambiguationData":[TD([[makeQuery(id+"F9.imprint","IMPRINT",EDGE,{"disambiguationData":[TD([[subQ5,-1.0]])],"derivedFrom":subQ0}),-1.0]])]});}
            var Q54;
            {var subQ0=sQuery(id+"F9.wireOp",EDGE,"E22.0.3");var subQ3=sQuery(id+"F9.wireOp",EDGE,"E23.0.0");var subQ5=makeQuery(id+"F9.imprint","INTERSECT",VERTEX,{"derivedFrom":[subQ0,subQ3]});Q54=makeQuery(id+"F9.imprint","IMPRINT",FACE,{"disambiguationData":[TD([[makeQuery(id+"F9.imprint","IMPRINT",EDGE,{"disambiguationData":[TD([[subQ5,-1.0]])],"derivedFrom":subQ0}),-1.0]])]});}
            var Q55;
            Q55=makeQuery(id+"F8.opPattern","COPY",FACE,{"derivedFrom":makeQuery(id+"F3.opExtrude","CAP_FACE",FACE,{"disambiguationData":[OSD([sQuery(id+"F0.wireOp",EDGE,"E0.left"),sQuery(id+"F0.wireOp",EDGE,"E0.right"),sQuery(id+"F0.wireOp",EDGE,"E1.0"),sQuery(id+"F0.wireOp",EDGE,"E1.1"),sQuery(id+"F0.wireOp",EDGE,"E1.2"),sQuery(id+"F0.wireOp",EDGE,"E1.3"),sQuery(id+"F2.wireOp",EDGE,"E2.0"),sQuery(id+"F2.wireOp",EDGE,"E3.0")])],"isStart":false}),"instanceName":"12"});
            extrude(context, id + "F10", {"entities" : qUnion([Q0, Q1, Q2, Q3, Q4, Q5, Q6, Q7, Q8, Q9, Q10, Q11, Q12, Q13, Q14, Q15, Q16, Q17, Q18, Q19, Q20, Q21, Q22, Q23, Q24, Q25, Q26, Q27, Q28, Q29, Q30, Q31, Q32, Q33, Q34, Q35, Q36, Q37, Q38, Q39, Q40, Q41, Q42, Q43, Q44, Q45, Q46, Q47, Q48, Q49, Q50, Q51, Q52, Q53, Q54]), "operationType" : NewBodyOperationType.ADD, "endBound" : BoundingType.UP_TO_SURFACE, "oppositeDirection" : true, "depth" : 25 * mm, "endBoundEntityFace" : qUnion([Q55]), "offsetDistance" : 25 * mm});
        }
        {
            var Q0;
            {var subQ0=sQuery(id+"F9.wireOp",EDGE,"E38.0.0");var subQ1=sQuery(id+"F9.wireOp",EDGE,"E12.0");var subQ2=sQuery(id+"F9.wireOp",EDGE,"E29.0.0");var subQ3=sQuery(id+"F9.wireOp",EDGE,"E28.0.0");var subQ4=sQuery(id+"F9.wireOp",EDGE,"E27.0.0");var subQ5=sQuery(id+"F9.wireOp",EDGE,"E26.0.0");var subQ6=sQuery(id+"F9.wireOp",EDGE,"E25.0.0");var subQ7=sQuery(id+"F9.wireOp",EDGE,"E24.0.0");var subQ8=sQuery(id+"F9.wireOp",EDGE,"E23.0.0");var subQ9=sQuery(id+"F9.wireOp",EDGE,"E22.0.0");var subQ10=sQuery(id+"F9.wireOp",EDGE,"E21.0.0");var subQ11=sQuery(id+"F9.wireOp",EDGE,"E20.0.0");var subQ12=sQuery(id+"F9.wireOp",EDGE,"E19.0.0");var subQ13=sQuery(id+"F9.wireOp",EDGE,"E18.0.0");var subQ14=sQuery(id+"F9.wireOp",EDGE,"E17.0.0");var subQ15=sQuery(id+"F9.wireOp",EDGE,"E16.0.0");var subQ16=sQuery(id+"F9.wireOp",EDGE,"E15.0.0");var subQ17=sQuery(id+"F9.wireOp",EDGE,"E14.0.0");var subQ18=sQuery(id+"F9.wireOp",EDGE,"E13.0.0");var subQ19=sQuery(id+"F9.wireOp",EDGE,"E37.0.0");var subQ20=sQuery(id+"F9.wireOp",EDGE,"E36.0.0");var subQ21=sQuery(id+"F9.wireOp",EDGE,"E35.0.0");var subQ22=sQuery(id+"F9.wireOp",EDGE,"E34.0.0");var subQ23=sQuery(id+"F9.wireOp",EDGE,"E33.0.0");var subQ24=sQuery(id+"F9.wireOp",EDGE,"E32.0.0");var subQ25=sQuery(id+"F9.wireOp",EDGE,"E31.0.0");var subQ26=sQuery(id+"F9.wireOp",EDGE,"E30.0.1");var subQ27=sQuery(id+"F9.wireOp",EDGE,"E39.0.0");var subQ28=sQuery(id+"F9.wireOp",EDGE,"E11");var subQ29=makeQuery(id+"F1.opExtrude","CAP_FACE",FACE,{"disambiguationData":[OSD([sQuery(id+"F0.wireOp",EDGE,"E0.bottom"),sQuery(id+"F0.wireOp",EDGE,"E0.top"),sQuery(id+"F0.wireOp",EDGE,"E0.left"),sQuery(id+"F0.wireOp",EDGE,"E0.right"),sQuery(id+"F0.wireOp",EDGE,"E1.0"),sQuery(id+"F0.wireOp",EDGE,"E1.1"),sQuery(id+"F0.wireOp",EDGE,"E1.2"),sQuery(id+"F0.wireOp",EDGE,"E1.3")])],"isStart":false});Q0=makeQuery(id+"F10.boolean.opBoolean","MERGE",FACE,{"derivedFrom":[subQ29,makeQuery(id+"F8.opPattern","COPY",FACE,{"derivedFrom":subQ29,"instanceName":"1"}),makeQuery(id+"F8.opPattern","COPY",FACE,{"derivedFrom":subQ29,"instanceName":"2"}),makeQuery(id+"F8.opPattern","COPY",FACE,{"derivedFrom":subQ29,"instanceName":"3"}),makeQuery(id+"F8.opPattern","COPY",FACE,{"derivedFrom":subQ29,"instanceName":"4"}),makeQuery(id+"F8.opPattern","COPY",FACE,{"derivedFrom":subQ29,"instanceName":"5"}),makeQuery(id+"F8.opPattern","COPY",FACE,{"derivedFrom":subQ29,"instanceName":"6"}),makeQuery(id+"F8.opPattern","COPY",FACE,{"derivedFrom":subQ29,"instanceName":"7"}),makeQuery(id+"F8.opPattern","COPY",FACE,{"derivedFrom":subQ29,"instanceName":"8"}),makeQuery(id+"F8.opPattern","COPY",FACE,{"derivedFrom":subQ29,"instanceName":"9"}),makeQuery(id+"F8.opPattern","COPY",FACE,{"derivedFrom":subQ29,"instanceName":"10"}),makeQuery(id+"F8.opPattern","COPY",FACE,{"derivedFrom":subQ29,"instanceName":"11"}),makeQuery(id+"F8.opPattern","COPY",FACE,{"derivedFrom":subQ29,"instanceName":"12"}),makeQuery(id+"F8.opPattern","COPY",FACE,{"derivedFrom":subQ29,"instanceName":"13"}),makeQuery(id+"F8.opPattern","COPY",FACE,{"derivedFrom":subQ29,"instanceName":"14"}),makeQuery(id+"F8.opPattern","COPY",FACE,{"derivedFrom":subQ29,"instanceName":"15"}),makeQuery(id+"F8.opPattern","COPY",FACE,{"derivedFrom":subQ29,"instanceName":"16"}),makeQuery(id+"F8.opPattern","COPY",FACE,{"derivedFrom":subQ29,"instanceName":"17"}),makeQuery(id+"F8.opPattern","COPY",FACE,{"derivedFrom":subQ29,"instanceName":"18"}),makeQuery(id+"F8.opPattern","COPY",FACE,{"derivedFrom":subQ29,"instanceName":"19"}),makeQuery(id+"F8.opPattern","COPY",FACE,{"derivedFrom":subQ29,"instanceName":"20"}),makeQuery(id+"F8.opPattern","COPY",FACE,{"derivedFrom":subQ29,"instanceName":"21"}),makeQuery(id+"F8.opPattern","COPY",FACE,{"derivedFrom":subQ29,"instanceName":"22"}),makeQuery(id+"F8.opPattern","COPY",FACE,{"derivedFrom":subQ29,"instanceName":"23"}),makeQuery(id+"F8.opPattern","COPY",FACE,{"derivedFrom":subQ29,"instanceName":"24"}),makeQuery(id+"F8.opPattern","COPY",FACE,{"derivedFrom":subQ29,"instanceName":"25"}),makeQuery(id+"F8.opPattern","COPY",FACE,{"derivedFrom":subQ29,"instanceName":"26"}),makeQuery(id+"F10.opExtrude","CAP_FACE",FACE,{"disambiguationData":[OSD([subQ28,sQuery(id+"F9.wireOp",EDGE,"E38.0.2"),subQ27,sQuery(id+"F9.wireOp",EDGE,"E39.0.1")])],"isStart":true}),makeQuery(id+"F10.opExtrude","CAP_FACE",FACE,{"disambiguationData":[OSD([subQ28,sQuery(id+"F9.wireOp",EDGE,"E39.0.2"),subQ26,sQuery(id+"F9.wireOp",EDGE,"E30.0.2")])],"isStart":true}),makeQuery(id+"F10.opExtrude","CAP_FACE",FACE,{"disambiguationData":[OSD([subQ28,subQ25,sQuery(id+"F9.wireOp",EDGE,"E31.0.1"),sQuery(id+"F9.wireOp",EDGE,"E30.0.3")])],"isStart":true}),makeQuery(id+"F10.opExtrude","CAP_FACE",FACE,{"disambiguationData":[OSD([subQ28,sQuery(id+"F9.wireOp",EDGE,"E31.0.2"),subQ24,sQuery(id+"F9.wireOp",EDGE,"E32.0.1")])],"isStart":true}),makeQuery(id+"F10.opExtrude","CAP_FACE",FACE,{"disambiguationData":[OSD([subQ28,sQuery(id+"F9.wireOp",EDGE,"E32.0.2"),subQ23,sQuery(id+"F9.wireOp",EDGE,"E33.0.1")])],"isStart":true}),makeQuery(id+"F10.opExtrude","CAP_FACE",FACE,{"disambiguationData":[OSD([subQ28,sQuery(id+"F9.wireOp",EDGE,"E33.0.2"),subQ22,sQuery(id+"F9.wireOp",EDGE,"E34.0.1")])],"isStart":true}),makeQuery(id+"F10.opExtrude","CAP_FACE",FACE,{"disambiguationData":[OSD([subQ28,sQuery(id+"F9.wireOp",EDGE,"E34.0.2"),subQ21,sQuery(id+"F9.wireOp",EDGE,"E35.0.1")])],"isStart":true}),makeQuery(id+"F10.opExtrude","CAP_FACE",FACE,{"disambiguationData":[OSD([subQ28,sQuery(id+"F9.wireOp",EDGE,"E35.0.2"),subQ20,sQuery(id+"F9.wireOp",EDGE,"E36.0.1")])],"isStart":true}),makeQuery(id+"F10.opExtrude","CAP_FACE",FACE,{"disambiguationData":[OSD([subQ28,sQuery(id+"F9.wireOp",EDGE,"E36.0.2"),subQ19,sQuery(id+"F9.wireOp",EDGE,"E37.0.1")])],"isStart":true}),makeQuery(id+"F10.opExtrude","CAP_FACE",FACE,{"disambiguationData":[OSD([subQ28,subQ18,sQuery(id+"F9.wireOp",EDGE,"E13.0.1"),sQuery(id+"F9.wireOp",EDGE,"E37.0.2")])],"isStart":true}),makeQuery(id+"F10.opExtrude","CAP_FACE",FACE,{"disambiguationData":[OSD([subQ28,sQuery(id+"F9.wireOp",EDGE,"E13.0.2"),subQ17,sQuery(id+"F9.wireOp",EDGE,"E14.0.1")])],"isStart":true}),makeQuery(id+"F10.opExtrude","CAP_FACE",FACE,{"disambiguationData":[OSD([subQ28,sQuery(id+"F9.wireOp",EDGE,"E14.0.2"),subQ16,sQuery(id+"F9.wireOp",EDGE,"E15.0.1")])],"isStart":true}),makeQuery(id+"F10.opExtrude","CAP_FACE",FACE,{"disambiguationData":[OSD([subQ28,sQuery(id+"F9.wireOp",EDGE,"E15.0.2"),subQ15,sQuery(id+"F9.wireOp",EDGE,"E16.0.1")])],"isStart":true}),makeQuery(id+"F10.opExtrude","CAP_FACE",FACE,{"disambiguationData":[OSD([subQ28,sQuery(id+"F9.wireOp",EDGE,"E16.0.2"),subQ14,sQuery(id+"F9.wireOp",EDGE,"E17.0.1")])],"isStart":true}),makeQuery(id+"F10.opExtrude","CAP_FACE",FACE,{"disambiguationData":[OSD([subQ28,sQuery(id+"F9.wireOp",EDGE,"E17.0.2"),subQ13,sQuery(id+"F9.wireOp",EDGE,"E18.0.1")])],"isStart":true}),makeQuery(id+"F10.opExtrude","CAP_FACE",FACE,{"disambiguationData":[OSD([subQ28,sQuery(id+"F9.wireOp",EDGE,"E18.0.2"),subQ12,sQuery(id+"F9.wireOp",EDGE,"E19.0.1")])],"isStart":true}),makeQuery(id+"F10.opExtrude","CAP_FACE",FACE,{"disambiguationData":[OSD([subQ28,sQuery(id+"F9.wireOp",EDGE,"E19.0.2"),subQ11,sQuery(id+"F9.wireOp",EDGE,"E20.0.1")])],"isStart":true}),makeQuery(id+"F10.opExtrude","CAP_FACE",FACE,{"disambiguationData":[OSD([subQ28,sQuery(id+"F9.wireOp",EDGE,"E20.0.2"),subQ10,sQuery(id+"F9.wireOp",EDGE,"E21.0.1")])],"isStart":true}),makeQuery(id+"F10.opExtrude","CAP_FACE",FACE,{"disambiguationData":[OSD([subQ28,sQuery(id+"F9.wireOp",EDGE,"E21.0.2"),subQ9,sQuery(id+"F9.wireOp",EDGE,"E22.0.1")])],"isStart":true}),makeQuery(id+"F10.opExtrude","CAP_FACE",FACE,{"disambiguationData":[OSD([subQ28,sQuery(id+"F9.wireOp",EDGE,"E22.0.2"),subQ8,sQuery(id+"F9.wireOp",EDGE,"E23.0.1")])],"isStart":true}),makeQuery(id+"F10.opExtrude","CAP_FACE",FACE,{"disambiguationData":[OSD([subQ28,sQuery(id+"F9.wireOp",EDGE,"E23.0.2"),subQ7,sQuery(id+"F9.wireOp",EDGE,"E24.0.1")])],"isStart":true}),makeQuery(id+"F10.opExtrude","CAP_FACE",FACE,{"disambiguationData":[OSD([subQ28,sQuery(id+"F9.wireOp",EDGE,"E24.0.2"),subQ6,sQuery(id+"F9.wireOp",EDGE,"E25.0.1")])],"isStart":true}),makeQuery(id+"F10.opExtrude","CAP_FACE",FACE,{"disambiguationData":[OSD([subQ28,sQuery(id+"F9.wireOp",EDGE,"E25.0.2"),subQ5,sQuery(id+"F9.wireOp",EDGE,"E26.0.1")])],"isStart":true}),makeQuery(id+"F10.opExtrude","CAP_FACE",FACE,{"disambiguationData":[OSD([subQ28,sQuery(id+"F9.wireOp",EDGE,"E26.0.2"),subQ4,sQuery(id+"F9.wireOp",EDGE,"E27.0.1")])],"isStart":true}),makeQuery(id+"F10.opExtrude","CAP_FACE",FACE,{"disambiguationData":[OSD([subQ28,sQuery(id+"F9.wireOp",EDGE,"E27.0.2"),subQ3,sQuery(id+"F9.wireOp",EDGE,"E28.0.1")])],"isStart":true}),makeQuery(id+"F10.opExtrude","CAP_FACE",FACE,{"disambiguationData":[OSD([subQ28,sQuery(id+"F9.wireOp",EDGE,"E28.0.2"),subQ2,sQuery(id+"F9.wireOp",EDGE,"E29.0.1")])],"isStart":true}),makeQuery(id+"F10.opExtrude","CAP_FACE",FACE,{"disambiguationData":[OSD([subQ28,sQuery(id+"F9.wireOp",EDGE,"E29.0.2"),subQ0,sQuery(id+"F9.wireOp",EDGE,"E38.0.1")])],"isStart":true}),makeQuery(id+"F10.opExtrude","CAP_FACE",FACE,{"disambiguationData":[OSD([subQ1,sQuery(id+"F9.wireOp",EDGE,"E38.0.3"),subQ27])],"isStart":true}),makeQuery(id+"F10.opExtrude","CAP_FACE",FACE,{"disambiguationData":[OSD([subQ1,sQuery(id+"F9.wireOp",EDGE,"E39.0.3"),subQ26])],"isStart":true}),makeQuery(id+"F10.opExtrude","CAP_FACE",FACE,{"disambiguationData":[OSD([subQ1,subQ25,sQuery(id+"F9.wireOp",EDGE,"E30.0.0")])],"isStart":true}),makeQuery(id+"F10.opExtrude","CAP_FACE",FACE,{"disambiguationData":[OSD([subQ1,sQuery(id+"F9.wireOp",EDGE,"E31.0.3"),subQ24])],"isStart":true}),makeQuery(id+"F10.opExtrude","CAP_FACE",FACE,{"disambiguationData":[OSD([subQ1,sQuery(id+"F9.wireOp",EDGE,"E32.0.3"),subQ23])],"isStart":true}),makeQuery(id+"F10.opExtrude","CAP_FACE",FACE,{"disambiguationData":[OSD([subQ1,sQuery(id+"F9.wireOp",EDGE,"E33.0.3"),subQ22])],"isStart":true}),makeQuery(id+"F10.opExtrude","CAP_FACE",FACE,{"disambiguationData":[OSD([subQ1,sQuery(id+"F9.wireOp",EDGE,"E34.0.3"),subQ21])],"isStart":true}),makeQuery(id+"F10.opExtrude","CAP_FACE",FACE,{"disambiguationData":[OSD([subQ1,sQuery(id+"F9.wireOp",EDGE,"E35.0.3"),subQ20])],"isStart":true}),makeQuery(id+"F10.opExtrude","CAP_FACE",FACE,{"disambiguationData":[OSD([subQ1,sQuery(id+"F9.wireOp",EDGE,"E36.0.3"),subQ19])],"isStart":true}),makeQuery(id+"F10.opExtrude","CAP_FACE",FACE,{"disambiguationData":[OSD([subQ1,subQ18,sQuery(id+"F9.wireOp",EDGE,"E37.0.3")])],"isStart":true}),makeQuery(id+"F10.opExtrude","CAP_FACE",FACE,{"disambiguationData":[OSD([subQ1,sQuery(id+"F9.wireOp",EDGE,"E13.0.3"),subQ17])],"isStart":true}),makeQuery(id+"F10.opExtrude","CAP_FACE",FACE,{"disambiguationData":[OSD([subQ1,sQuery(id+"F9.wireOp",EDGE,"E14.0.3"),subQ16])],"isStart":true}),makeQuery(id+"F10.opExtrude","CAP_FACE",FACE,{"disambiguationData":[OSD([subQ1,sQuery(id+"F9.wireOp",EDGE,"E15.0.3"),subQ15])],"isStart":true}),makeQuery(id+"F10.opExtrude","CAP_FACE",FACE,{"disambiguationData":[OSD([subQ1,sQuery(id+"F9.wireOp",EDGE,"E16.0.3"),subQ14])],"isStart":true}),makeQuery(id+"F10.opExtrude","CAP_FACE",FACE,{"disambiguationData":[OSD([subQ1,sQuery(id+"F9.wireOp",EDGE,"E17.0.3"),subQ13])],"isStart":true}),makeQuery(id+"F10.opExtrude","CAP_FACE",FACE,{"disambiguationData":[OSD([subQ1,sQuery(id+"F9.wireOp",EDGE,"E18.0.3"),subQ12])],"isStart":true}),makeQuery(id+"F10.opExtrude","CAP_FACE",FACE,{"disambiguationData":[OSD([subQ1,sQuery(id+"F9.wireOp",EDGE,"E19.0.3"),subQ11])],"isStart":true}),makeQuery(id+"F10.opExtrude","CAP_FACE",FACE,{"disambiguationData":[OSD([subQ1,sQuery(id+"F9.wireOp",EDGE,"E20.0.3"),subQ10])],"isStart":true}),makeQuery(id+"F10.opExtrude","CAP_FACE",FACE,{"disambiguationData":[OSD([subQ1,sQuery(id+"F9.wireOp",EDGE,"E21.0.3"),subQ9])],"isStart":true}),makeQuery(id+"F10.opExtrude","CAP_FACE",FACE,{"disambiguationData":[OSD([subQ1,sQuery(id+"F9.wireOp",EDGE,"E22.0.3"),subQ8])],"isStart":true}),makeQuery(id+"F10.opExtrude","CAP_FACE",FACE,{"disambiguationData":[OSD([subQ1,sQuery(id+"F9.wireOp",EDGE,"E23.0.3"),subQ7])],"isStart":true}),makeQuery(id+"F10.opExtrude","CAP_FACE",FACE,{"disambiguationData":[OSD([subQ1,sQuery(id+"F9.wireOp",EDGE,"E24.0.3"),subQ6])],"isStart":true}),makeQuery(id+"F10.opExtrude","CAP_FACE",FACE,{"disambiguationData":[OSD([subQ1,sQuery(id+"F9.wireOp",EDGE,"E25.0.3"),subQ5])],"isStart":true}),makeQuery(id+"F10.opExtrude","CAP_FACE",FACE,{"disambiguationData":[OSD([subQ1,sQuery(id+"F9.wireOp",EDGE,"E26.0.3"),subQ4])],"isStart":true}),makeQuery(id+"F10.opExtrude","CAP_FACE",FACE,{"disambiguationData":[OSD([subQ1,sQuery(id+"F9.wireOp",EDGE,"E27.0.3"),subQ3])],"isStart":true}),makeQuery(id+"F10.opExtrude","CAP_FACE",FACE,{"disambiguationData":[OSD([subQ1,sQuery(id+"F9.wireOp",EDGE,"E28.0.3"),subQ2])],"isStart":true}),makeQuery(id+"F10.opExtrude","CAP_FACE",FACE,{"disambiguationData":[OSD([subQ1,sQuery(id+"F9.wireOp",EDGE,"E29.0.3"),subQ0])],"isStart":true})]});}
            var sketch = newSketch(context, id + "F11", { "sketchPlane" : qUnion([Q0])});
            skCircle(sketch, "E40", {"center": v(-59.6, -41.02) * mm, "radius": 70 * mm});
            skCircle(sketch, "E41", {"center": v(-59.6, -41.02) * mm, "radius": 88.5 * mm});
            skSolve(sketch);
        }
        {
            var Q0;
            Q0=makeQuery(id+"F11.imprint","IMPRINT",FACE,{"disambiguationData":[TD([[makeQuery(id+"F11.imprint","IMPRINT",EDGE,{"derivedFrom":sQuery(id+"F11.wireOp",EDGE,"E41")}),-1.0]])]});
            var Q1;
            Q1=makeQuery(id+"F11.imprint","IMPRINT",FACE,{"disambiguationData":[TD([[makeQuery(id+"F11.imprint","IMPRINT",EDGE,{"derivedFrom":sQuery(id+"F11.wireOp",EDGE,"E40")}),1.0]])]});
            extrude(context, id + "F12", {"entities" : qUnion([Q0, Q1]), "operationType" : NewBodyOperationType.REMOVE, "oppositeDirection" : true, "depth" : 25 * mm, "offsetDistance" : 25 * mm});
        }
        {
            var Q0;
            {var subQ0=sQuery(id+"F2.wireOp",EDGE,"E5.0");var subQ1=sQuery(id+"F2.wireOp",EDGE,"E3.0");var subQ2=sQuery(id+"F2.wireOp",EDGE,"E2.0");var subQ3=sQuery(id+"F0.wireOp",EDGE,"E1.3");var subQ4=sQuery(id+"F0.wireOp",EDGE,"E1.2");var subQ5=sQuery(id+"F0.wireOp",EDGE,"E1.1");var subQ6=sQuery(id+"F0.wireOp",EDGE,"E1.0");var subQ7=sQuery(id+"F0.wireOp",EDGE,"E0.left");var subQ8=makeQuery(id+"F3.opExtrude","CAP_FACE",FACE,{"disambiguationData":[OSD([subQ7,subQ6,subQ5,subQ4,subQ3,subQ2,subQ1,subQ0])],"isStart":false});Q0=makeQuery(id+"F10.boolean.opBoolean","MERGE",FACE,{"derivedFrom":[subQ8,makeQuery(id+"F8.opPattern","COPY",FACE,{"derivedFrom":subQ8,"instanceName":"1"}),makeQuery(id+"F8.opPattern","COPY",FACE,{"derivedFrom":subQ8,"instanceName":"2"}),makeQuery(id+"F8.opPattern","COPY",FACE,{"derivedFrom":subQ8,"instanceName":"3"}),makeQuery(id+"F8.opPattern","COPY",FACE,{"derivedFrom":subQ8,"instanceName":"4"}),makeQuery(id+"F8.opPattern","COPY",FACE,{"derivedFrom":subQ8,"instanceName":"5"}),makeQuery(id+"F8.opPattern","COPY",FACE,{"derivedFrom":subQ8,"instanceName":"6"}),makeQuery(id+"F8.opPattern","COPY",FACE,{"derivedFrom":subQ8,"instanceName":"7"}),makeQuery(id+"F8.opPattern","COPY",FACE,{"derivedFrom":subQ8,"instanceName":"8"}),makeQuery(id+"F8.opPattern","COPY",FACE,{"derivedFrom":subQ8,"instanceName":"9"}),makeQuery(id+"F8.opPattern","COPY",FACE,{"derivedFrom":subQ8,"instanceName":"10"}),makeQuery(id+"F8.opPattern","COPY",FACE,{"derivedFrom":subQ8,"instanceName":"11"}),makeQuery(id+"F8.opPattern","COPY",FACE,{"derivedFrom":subQ8,"instanceName":"12"}),makeQuery(id+"F8.opPattern","COPY",FACE,{"derivedFrom":subQ8,"instanceName":"13"}),makeQuery(id+"F8.opPattern","COPY",FACE,{"derivedFrom":subQ8,"instanceName":"14"}),makeQuery(id+"F8.opPattern","COPY",FACE,{"derivedFrom":subQ8,"instanceName":"15"}),makeQuery(id+"F8.opPattern","COPY",FACE,{"derivedFrom":subQ8,"instanceName":"16"}),makeQuery(id+"F8.opPattern","COPY",FACE,{"derivedFrom":subQ8,"instanceName":"17"}),makeQuery(id+"F8.opPattern","COPY",FACE,{"derivedFrom":subQ8,"instanceName":"18"}),makeQuery(id+"F8.opPattern","COPY",FACE,{"derivedFrom":subQ8,"instanceName":"19"}),makeQuery(id+"F8.opPattern","COPY",FACE,{"derivedFrom":subQ8,"instanceName":"20"}),makeQuery(id+"F8.opPattern","COPY",FACE,{"derivedFrom":subQ8,"instanceName":"21"}),makeQuery(id+"F8.opPattern","COPY",FACE,{"derivedFrom":subQ8,"instanceName":"22"}),makeQuery(id+"F8.opPattern","COPY",FACE,{"derivedFrom":subQ8,"instanceName":"23"}),makeQuery(id+"F8.opPattern","COPY",FACE,{"derivedFrom":subQ8,"instanceName":"24"}),makeQuery(id+"F8.opPattern","COPY",FACE,{"derivedFrom":subQ8,"instanceName":"25"}),makeQuery(id+"F8.opPattern","COPY",FACE,{"derivedFrom":subQ8,"instanceName":"26"}),makeQuery(id+"F10.opExtrude","CAP_FACE",FACE,{"disambiguationData":[OSD([subQ7,subQ6,subQ5,subQ4,subQ3,subQ2,subQ1,subQ0]),OD(0.0)],"isStart":false}),makeQuery(id+"F10.opExtrude","CAP_FACE",FACE,{"disambiguationData":[OSD([subQ7,subQ6,subQ5,subQ4,subQ3,subQ2,subQ1,subQ0]),OD(1.0)],"isStart":false}),makeQuery(id+"F10.opExtrude","CAP_FACE",FACE,{"disambiguationData":[OSD([subQ7,subQ6,subQ5,subQ4,subQ3,subQ2,subQ1,subQ0]),OD(2.0)],"isStart":false}),makeQuery(id+"F10.opExtrude","CAP_FACE",FACE,{"disambiguationData":[OSD([subQ7,subQ6,subQ5,subQ4,subQ3,subQ2,subQ1,subQ0]),OD(3.0)],"isStart":false}),makeQuery(id+"F10.opExtrude","CAP_FACE",FACE,{"disambiguationData":[OSD([subQ7,subQ6,subQ5,subQ4,subQ3,subQ2,subQ1,subQ0]),OD(4.0)],"isStart":false}),makeQuery(id+"F10.opExtrude","CAP_FACE",FACE,{"disambiguationData":[OSD([subQ7,subQ6,subQ5,subQ4,subQ3,subQ2,subQ1,subQ0]),OD(5.0)],"isStart":false}),makeQuery(id+"F10.opExtrude","CAP_FACE",FACE,{"disambiguationData":[OSD([subQ7,subQ6,subQ5,subQ4,subQ3,subQ2,subQ1,subQ0]),OD(6.0)],"isStart":false}),makeQuery(id+"F10.opExtrude","CAP_FACE",FACE,{"disambiguationData":[OSD([subQ7,subQ6,subQ5,subQ4,subQ3,subQ2,subQ1,subQ0]),OD(7.0)],"isStart":false}),makeQuery(id+"F10.opExtrude","CAP_FACE",FACE,{"disambiguationData":[OSD([subQ7,subQ6,subQ5,subQ4,subQ3,subQ2,subQ1,subQ0]),OD(8.0)],"isStart":false}),makeQuery(id+"F10.opExtrude","CAP_FACE",FACE,{"disambiguationData":[OSD([subQ7,subQ6,subQ5,subQ4,subQ3,subQ2,subQ1,subQ0]),OD(9.0)],"isStart":false}),makeQuery(id+"F10.opExtrude","CAP_FACE",FACE,{"disambiguationData":[OSD([subQ7,subQ6,subQ5,subQ4,subQ3,subQ2,subQ1,subQ0]),OD(10.0)],"isStart":false}),makeQuery(id+"F10.opExtrude","CAP_FACE",FACE,{"disambiguationData":[OSD([subQ7,subQ6,subQ5,subQ4,subQ3,subQ2,subQ1,subQ0]),OD(11.0)],"isStart":false}),makeQuery(id+"F10.opExtrude","CAP_FACE",FACE,{"disambiguationData":[OSD([subQ7,subQ6,subQ5,subQ4,subQ3,subQ2,subQ1,subQ0]),OD(12.0)],"isStart":false}),makeQuery(id+"F10.opExtrude","CAP_FACE",FACE,{"disambiguationData":[OSD([subQ7,subQ6,subQ5,subQ4,subQ3,subQ2,subQ1,subQ0]),OD(13.0)],"isStart":false}),makeQuery(id+"F10.opExtrude","CAP_FACE",FACE,{"disambiguationData":[OSD([subQ7,subQ6,subQ5,subQ4,subQ3,subQ2,subQ1,subQ0]),OD(14.0)],"isStart":false}),makeQuery(id+"F10.opExtrude","CAP_FACE",FACE,{"disambiguationData":[OSD([subQ7,subQ6,subQ5,subQ4,subQ3,subQ2,subQ1,subQ0]),OD(15.0)],"isStart":false}),makeQuery(id+"F10.opExtrude","CAP_FACE",FACE,{"disambiguationData":[OSD([subQ7,subQ6,subQ5,subQ4,subQ3,subQ2,subQ1,subQ0]),OD(16.0)],"isStart":false}),makeQuery(id+"F10.opExtrude","CAP_FACE",FACE,{"disambiguationData":[OSD([subQ7,subQ6,subQ5,subQ4,subQ3,subQ2,subQ1,subQ0]),OD(17.0)],"isStart":false}),makeQuery(id+"F10.opExtrude","CAP_FACE",FACE,{"disambiguationData":[OSD([subQ7,subQ6,subQ5,subQ4,subQ3,subQ2,subQ1,subQ0]),OD(18.0)],"isStart":false}),makeQuery(id+"F10.opExtrude","CAP_FACE",FACE,{"disambiguationData":[OSD([subQ7,subQ6,subQ5,subQ4,subQ3,subQ2,subQ1,subQ0]),OD(19.0)],"isStart":false}),makeQuery(id+"F10.opExtrude","CAP_FACE",FACE,{"disambiguationData":[OSD([subQ7,subQ6,subQ5,subQ4,subQ3,subQ2,subQ1,subQ0]),OD(20.0)],"isStart":false}),makeQuery(id+"F10.opExtrude","CAP_FACE",FACE,{"disambiguationData":[OSD([subQ7,subQ6,subQ5,subQ4,subQ3,subQ2,subQ1,subQ0]),OD(21.0)],"isStart":false}),makeQuery(id+"F10.opExtrude","CAP_FACE",FACE,{"disambiguationData":[OSD([subQ7,subQ6,subQ5,subQ4,subQ3,subQ2,subQ1,subQ0]),OD(22.0)],"isStart":false}),makeQuery(id+"F10.opExtrude","CAP_FACE",FACE,{"disambiguationData":[OSD([subQ7,subQ6,subQ5,subQ4,subQ3,subQ2,subQ1,subQ0]),OD(23.0)],"isStart":false}),makeQuery(id+"F10.opExtrude","CAP_FACE",FACE,{"disambiguationData":[OSD([subQ7,subQ6,subQ5,subQ4,subQ3,subQ2,subQ1,subQ0]),OD(24.0)],"isStart":false}),makeQuery(id+"F10.opExtrude","CAP_FACE",FACE,{"disambiguationData":[OSD([subQ7,subQ6,subQ5,subQ4,subQ3,subQ2,subQ1,subQ0]),OD(25.0)],"isStart":false}),makeQuery(id+"F10.opExtrude","CAP_FACE",FACE,{"disambiguationData":[OSD([subQ7,subQ6,subQ5,subQ4,subQ3,subQ2,subQ1,subQ0]),OD(26.0)],"isStart":false}),makeQuery(id+"F10.opExtrude","CAP_FACE",FACE,{"disambiguationData":[OSD([subQ7,subQ6,subQ5,subQ4,subQ3,subQ2,subQ1,subQ0]),OD(27.0)],"isStart":false}),makeQuery(id+"F10.opExtrude","CAP_FACE",FACE,{"disambiguationData":[OSD([subQ7,subQ6,subQ5,subQ4,subQ3,subQ2,subQ1,subQ0]),OD(28.0)],"isStart":false}),makeQuery(id+"F10.opExtrude","CAP_FACE",FACE,{"disambiguationData":[OSD([subQ7,subQ6,subQ5,subQ4,subQ3,subQ2,subQ1,subQ0]),OD(29.0)],"isStart":false}),makeQuery(id+"F10.opExtrude","CAP_FACE",FACE,{"disambiguationData":[OSD([subQ7,subQ6,subQ5,subQ4,subQ3,subQ2,subQ1,subQ0]),OD(30.0)],"isStart":false}),makeQuery(id+"F10.opExtrude","CAP_FACE",FACE,{"disambiguationData":[OSD([subQ7,subQ6,subQ5,subQ4,subQ3,subQ2,subQ1,subQ0]),OD(31.0)],"isStart":false}),makeQuery(id+"F10.opExtrude","CAP_FACE",FACE,{"disambiguationData":[OSD([subQ7,subQ6,subQ5,subQ4,subQ3,subQ2,subQ1,subQ0]),OD(32.0)],"isStart":false}),makeQuery(id+"F10.opExtrude","CAP_FACE",FACE,{"disambiguationData":[OSD([subQ7,subQ6,subQ5,subQ4,subQ3,subQ2,subQ1,subQ0]),OD(33.0)],"isStart":false}),makeQuery(id+"F10.opExtrude","CAP_FACE",FACE,{"disambiguationData":[OSD([subQ7,subQ6,subQ5,subQ4,subQ3,subQ2,subQ1,subQ0]),OD(34.0)],"isStart":false}),makeQuery(id+"F10.opExtrude","CAP_FACE",FACE,{"disambiguationData":[OSD([subQ7,subQ6,subQ5,subQ4,subQ3,subQ2,subQ1,subQ0]),OD(35.0)],"isStart":false}),makeQuery(id+"F10.opExtrude","CAP_FACE",FACE,{"disambiguationData":[OSD([subQ7,subQ6,subQ5,subQ4,subQ3,subQ2,subQ1,subQ0]),OD(36.0)],"isStart":false}),makeQuery(id+"F10.opExtrude","CAP_FACE",FACE,{"disambiguationData":[OSD([subQ7,subQ6,subQ5,subQ4,subQ3,subQ2,subQ1,subQ0]),OD(37.0)],"isStart":false}),makeQuery(id+"F10.opExtrude","CAP_FACE",FACE,{"disambiguationData":[OSD([subQ7,subQ6,subQ5,subQ4,subQ3,subQ2,subQ1,subQ0]),OD(38.0)],"isStart":false}),makeQuery(id+"F10.opExtrude","CAP_FACE",FACE,{"disambiguationData":[OSD([subQ7,subQ6,subQ5,subQ4,subQ3,subQ2,subQ1,subQ0]),OD(39.0)],"isStart":false}),makeQuery(id+"F10.opExtrude","CAP_FACE",FACE,{"disambiguationData":[OSD([subQ7,subQ6,subQ5,subQ4,subQ3,subQ2,subQ1,subQ0]),OD(40.0)],"isStart":false}),makeQuery(id+"F10.opExtrude","CAP_FACE",FACE,{"disambiguationData":[OSD([subQ7,subQ6,subQ5,subQ4,subQ3,subQ2,subQ1,subQ0]),OD(41.0)],"isStart":false}),makeQuery(id+"F10.opExtrude","CAP_FACE",FACE,{"disambiguationData":[OSD([subQ7,subQ6,subQ5,subQ4,subQ3,subQ2,subQ1,subQ0]),OD(42.0)],"isStart":false}),makeQuery(id+"F10.opExtrude","CAP_FACE",FACE,{"disambiguationData":[OSD([subQ7,subQ6,subQ5,subQ4,subQ3,subQ2,subQ1,subQ0]),OD(43.0)],"isStart":false}),makeQuery(id+"F10.opExtrude","CAP_FACE",FACE,{"disambiguationData":[OSD([subQ7,subQ6,subQ5,subQ4,subQ3,subQ2,subQ1,subQ0]),OD(44.0)],"isStart":false}),makeQuery(id+"F10.opExtrude","CAP_FACE",FACE,{"disambiguationData":[OSD([subQ7,subQ6,subQ5,subQ4,subQ3,subQ2,subQ1,subQ0]),OD(45.0)],"isStart":false}),makeQuery(id+"F10.opExtrude","CAP_FACE",FACE,{"disambiguationData":[OSD([subQ7,subQ6,subQ5,subQ4,subQ3,subQ2,subQ1,subQ0]),OD(46.0)],"isStart":false}),makeQuery(id+"F10.opExtrude","CAP_FACE",FACE,{"disambiguationData":[OSD([subQ7,subQ6,subQ5,subQ4,subQ3,subQ2,subQ1,subQ0]),OD(47.0)],"isStart":false}),makeQuery(id+"F10.opExtrude","CAP_FACE",FACE,{"disambiguationData":[OSD([subQ7,subQ6,subQ5,subQ4,subQ3,subQ2,subQ1,subQ0]),OD(48.0)],"isStart":false}),makeQuery(id+"F10.opExtrude","CAP_FACE",FACE,{"disambiguationData":[OSD([subQ7,subQ6,subQ5,subQ4,subQ3,subQ2,subQ1,subQ0]),OD(49.0)],"isStart":false}),makeQuery(id+"F10.opExtrude","CAP_FACE",FACE,{"disambiguationData":[OSD([subQ7,subQ6,subQ5,subQ4,subQ3,subQ2,subQ1,subQ0]),OD(50.0)],"isStart":false}),makeQuery(id+"F10.opExtrude","CAP_FACE",FACE,{"disambiguationData":[OSD([subQ7,subQ6,subQ5,subQ4,subQ3,subQ2,subQ1,subQ0]),OD(51.0)],"isStart":false}),makeQuery(id+"F10.opExtrude","CAP_FACE",FACE,{"disambiguationData":[OSD([subQ7,subQ6,subQ5,subQ4,subQ3,subQ2,subQ1,subQ0]),OD(52.0)],"isStart":false}),makeQuery(id+"F10.opExtrude","CAP_FACE",FACE,{"disambiguationData":[OSD([subQ7,subQ6,subQ5,subQ4,subQ3,subQ2,subQ1,subQ0]),OD(53.0)],"isStart":false})]});}
            var sketch = newSketch(context, id + "F13", { "sketchPlane" : qUnion([Q0])});
            skCircle(sketch, "E42.0", {"center": v(-59.6, 41.02) * mm, "radius": 70 * mm});
            skCircle(sketch, "E43.0", {"center": v(-59.6, 41.02) * mm, "radius": 88.5 * mm});
            skCircle(sketch, "E44.0", {"center": v(-59.6, 41.02) * mm, "radius": 69.85 * mm});
            skCircle(sketch, "E45.0", {"center": v(-59.6, 41.02) * mm, "radius": 67.85 * mm});
            skCircle(sketch, "E46.0", {"center": v(-59.6, 41.02) * mm, "radius": 88.65 * mm});
            skCircle(sketch, "E47.0", {"center": v(-59.6, 41.02) * mm, "radius": 90.65 * mm});
            skSolve(sketch);
        }
        {
            var Q0;
            Q0=makeQuery(id+"F13.imprint","IMPRINT",FACE,{"disambiguationData":[TD([[makeQuery(id+"F13.imprint","IMPRINT",EDGE,{"derivedFrom":sQuery(id+"F13.wireOp",EDGE,"E44.0")}),1.0]])]});
            var Q1;
            Q1=makeQuery(id+"F13.imprint","IMPRINT",FACE,{"disambiguationData":[TD([[makeQuery(id+"F13.imprint","IMPRINT",EDGE,{"derivedFrom":sQuery(id+"F13.wireOp",EDGE,"E46.0")}),-1.0]])]});
            extrude(context, id + "F14", {"entities" : qUnion([Q0, Q1]), "depth" : 10 * mm, "offsetDistance" : 25 * mm});
        }
        {
            var Q0;
            Q0=makeQuery(id+"F14.opExtrude","CAP_FACE",FACE,{"disambiguationData":[OSD([sQuery(id+"F13.wireOp",EDGE,"E46.0"),sQuery(id+"F13.wireOp",EDGE,"E47.0")])],"isStart":false});
            var sketch = newSketch(context, id + "F15", { "sketchPlane" : qUnion([Q0])});
            skCircle(sketch, "E48.0", {"center": v(-59.6, 41.02) * mm, "radius": 90.65 * mm});
            skCircle(sketch, "E49.0", {"center": v(-59.6, 41.02) * mm, "radius": 67.85 * mm});
            skSolve(sketch);
        }
        {
            var Q0;
            Q0 = qSketchRegion(id + "F15", true);
            extrude(context, id + "F16", {"entities" : qUnion([Q0]), "operationType" : NewBodyOperationType.ADD, "depth" : 2.1 * mm, "offsetDistance" : 25 * mm});
        }
        {
            var Q0;
            Q0=qCreatedBy(makeId("Right.planeOp"),FACE);
            cPlane(context, id + "F17", {"entities" : qUnion([Q0]), "cplaneType" : CPlaneType.OFFSET, "offset" : 25 * mm, "width" : 150 * mm, "height" : 150 * mm});
        }
        {
            var Q0;
            Q0=qCreatedBy(id+"F17.planeOp",FACE);
            var sketch = newSketch(context, id + "F18", { "sketchPlane" : qUnion([Q0])});
            skLineSegment(sketch, "E50.0", {"start": v(49.63, -22.1) * mm, "end": v(-131.67, -22.1) * mm});
            skLineSegment(sketch, "E51", {"start": v(-41.02, -22.1) * mm, "end": v(-41.02, -8.15) * mm});
            skLineSegment(sketch, "E52.0", {"start": v(-36.02, -22.1) * mm, "end": v(-36.02, -8.15) * mm});
            skLineSegment(sketch, "E53.0", {"start": v(-46.02, -22.1) * mm, "end": v(-46.02, -8.15) * mm});
            skLineSegment(sketch, "E54.0", {"start": v(49.63, -10) * mm, "end": v(-131.67, -10) * mm});
            skLineSegment(sketch, "E55.0", {"start": v(47.63, -20) * mm, "end": v(-129.67, -20) * mm});
            skSolve(sketch);
        }
        {
            var Q0;
            {var subQ0=sQuery(id+"F18.wireOp",EDGE,"E54.0");var subQ1=sQuery(id+"F18.wireOp",EDGE,"E51");var subQ2=makeQuery(id+"F18.imprint","INTERSECT",VERTEX,{"derivedFrom":[subQ1,subQ0]});Q0=makeQuery(id+"F18.imprint","IMPRINT",FACE,{"disambiguationData":[TD([[makeQuery(id+"F18.imprint","IMPRINT",EDGE,{"disambiguationData":[TD([[subQ2,1.0]])],"derivedFrom":subQ1}),1.0]])]});}
            var Q1;
            {var subQ0=sQuery(id+"F18.wireOp",EDGE,"E54.0");var subQ1=sQuery(id+"F18.wireOp",EDGE,"E51");var subQ2=makeQuery(id+"F18.imprint","INTERSECT",VERTEX,{"derivedFrom":[subQ1,subQ0]});Q1=makeQuery(id+"F18.imprint","IMPRINT",FACE,{"disambiguationData":[TD([[makeQuery(id+"F18.imprint","IMPRINT",EDGE,{"disambiguationData":[TD([[subQ2,1.0]])],"derivedFrom":subQ1}),-1.0]])]});}
            extrude(context, id + "F19", {"entities" : qUnion([Q0, Q1]), "operationType" : NewBodyOperationType.REMOVE, "depth" : 25 * mm, "offsetDistance" : 25 * mm});
        }
    });
